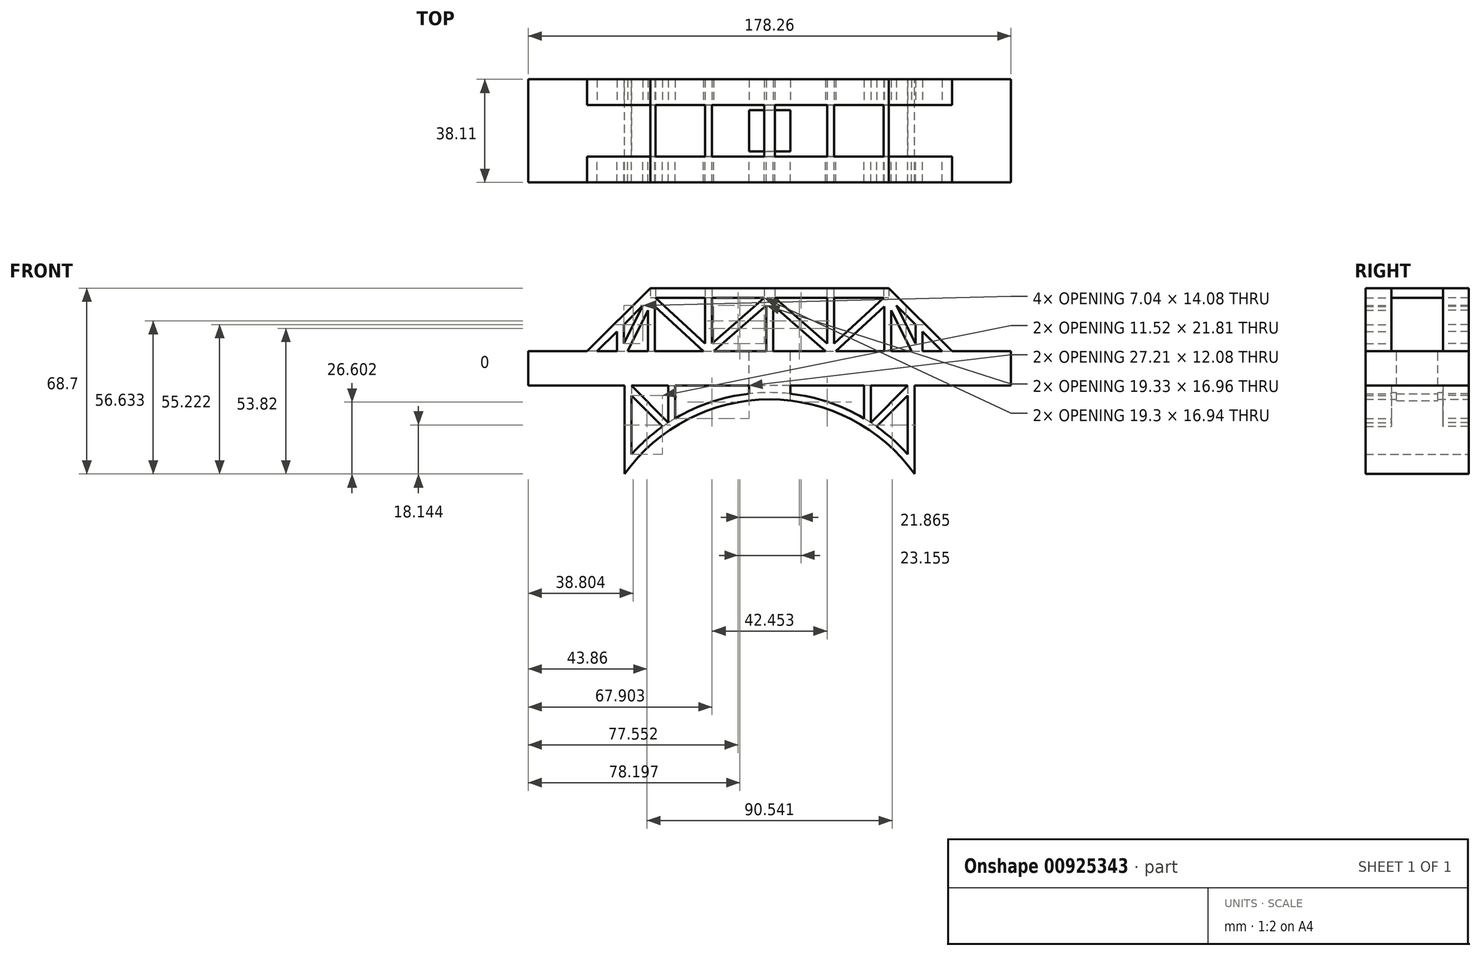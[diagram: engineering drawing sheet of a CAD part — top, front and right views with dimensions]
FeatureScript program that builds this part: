
annotation { "Feature Type Name" : "Feature", "Feature Type Description" : "" }
export const myFeature = defineFeature(function(context is Context, id is Id, definition is map)
    precondition{}
    {
        {
            var Q0;
            Q0=qCreatedBy(makeId("Front.planeOp"),FACE);
            var sketch = newSketch(context, id + "F0", { "sketchPlane" : qUnion([Q0])});
            skLineSegment(sketch, "E0.bottom", {"start": v(-63.73, 4.53) * mm, "end": v(63.73, 4.53) * mm});
            skLineSegment(sketch, "E1.bottom", {"start": v(-63.73, 4.53) * mm, "end": v(-89.13, 4.53) * mm});
            skLineSegment(sketch, "E1.top", {"start": v(-63.73, -8.17) * mm, "end": v(-89.13, -8.17) * mm});
            skLineSegment(sketch, "E1.left", {"start": v(-63.73, -3.37) * mm, "end": v(-63.73, -8.17) * mm});
            skLineSegment(sketch, "E1.right", {"start": v(-89.13, 4.53) * mm, "end": v(-89.13, -8.17) * mm});
            skPoint(sketch, "E2.oppositeSnap0", {"position": v(-76.43, -8.17) * mm});
            skLineSegment(sketch, "E2.bottom", {"start": v(63.73, 4.53) * mm, "end": v(89.13, 4.53) * mm});
            skLineSegment(sketch, "E2.top", {"start": v(63.73, -8.17) * mm, "end": v(89.13, -8.17) * mm});
            skLineSegment(sketch, "E2.left", {"start": v(63.73, 4.53) * mm, "end": v(63.73, -8.17) * mm});
            skLineSegment(sketch, "E2.right", {"start": v(89.13, 4.53) * mm, "end": v(89.13, -8.17) * mm});
            skPoint(sketch, "E3", {"position": v(-3.25, -27.46) * mm});
            skPoint(sketch, "E4", {"position": v(-24.97, -27.46) * mm});
            skPoint(sketch, "E5", {"position": v(18.48, -27.46) * mm});
            skPoint(sketch, "E6", {"position": v(0, -8.17) * mm});
            skPoint(sketch, "E7", {"position": v(-22.52, -8.17) * mm});
            skPoint(sketch, "E8", {"position": v(22.52, -8.17) * mm});
            skLineSegment(sketch, "E9", {"start": v(-43.58, -8.17) * mm, "end": v(-43.58, 4.53) * mm});
            skLineSegment(sketch, "E10", {"start": v(-22.52, -8.17) * mm, "end": v(-22.52, 4.53) * mm});
            skLineSegment(sketch, "E11", {"start": v(0, -8.17) * mm, "end": v(0, 4.53) * mm});
            skLineSegment(sketch, "E12", {"start": v(22.52, -8.17) * mm, "end": v(22.52, 4.53) * mm});
            skLineSegment(sketch, "E13", {"start": v(43.58, -8.17) * mm, "end": v(43.58, 4.53) * mm});
            skLineSegment(sketch, "E14", {"start": v(-63.73, 4.53) * mm, "end": v(-63.73, 4.53) * mm});
            skLineSegment(sketch, "E15", {"start": v(-63.73, -3.37) * mm, "end": v(-63.73, 4.53) * mm});
            skLineSegment(sketch, "E16", {"start": v(63.73, 4.53) * mm, "end": v(43.97, 24.3) * mm});
            skLineSegment(sketch, "E17", {"start": v(43.97, 24.3) * mm, "end": v(-43.97, 24.3) * mm});
            skLineSegment(sketch, "E18", {"start": v(-43.97, 24.3) * mm, "end": v(-63.73, 4.53) * mm});
            skLineSegment(sketch, "E19", {"start": v(-53.85, 14.41) * mm, "end": v(-53.85, 4.53) * mm});
            skLineSegment(sketch, "E20", {"start": v(-53.85, 4.53) * mm, "end": v(-43.97, 24.3) * mm});
            skLineSegment(sketch, "E21", {"start": v(53.85, 14.41) * mm, "end": v(53.85, 4.53) * mm});
            skLineSegment(sketch, "E22", {"start": v(43.97, 24.3) * mm, "end": v(53.85, 4.53) * mm});
            skLineSegment(sketch, "E23", {"start": v(43.97, 24.3) * mm, "end": v(22.52, 4.53) * mm});
            skLineSegment(sketch, "E24", {"start": v(0, 24.3) * mm, "end": v(22.52, 4.53) * mm});
            skLineSegment(sketch, "E25", {"start": v(-22.52, 4.53) * mm, "end": v(0, 24.3) * mm});
            skLineSegment(sketch, "E26", {"start": v(-43.97, 24.3) * mm, "end": v(-22.52, 4.53) * mm});
            skLineSegment(sketch, "E27.0", {"start": v(43.58, 22.22) * mm, "end": v(52.43, 4.53) * mm});
            skLineSegment(sketch, "E27.1", {"start": v(43.58, 22.22) * mm, "end": v(24.4, 4.53) * mm});
            skLineSegment(sketch, "E27.2", {"start": v(-52.43, 4.53) * mm, "end": v(-43.58, 22.22) * mm});
            skLineSegment(sketch, "E27.3", {"start": v(-43.58, 22.22) * mm, "end": v(-24.4, 4.53) * mm});
            skLineSegment(sketch, "E27.4", {"start": v(-20.6, 4.53) * mm, "end": v(0, 22.6) * mm});
            skLineSegment(sketch, "E27.5", {"start": v(0, 22.6) * mm, "end": v(20.6, 4.53) * mm});
            skLineSegment(sketch, "E28.0", {"start": v(42.1, 24.3) * mm, "end": v(22.5, 6.24) * mm});
            skLineSegment(sketch, "E28.1", {"start": v(1.93, 24.3) * mm, "end": v(22.5, 6.24) * mm});
            skLineSegment(sketch, "E28.2", {"start": v(-22.5, 6.24) * mm, "end": v(-1.93, 24.3) * mm});
            skLineSegment(sketch, "E28.3", {"start": v(-42.1, 24.3) * mm, "end": v(-22.5, 6.24) * mm});
            skLineSegment(sketch, "E29.0", {"start": v(-43.97, 27.89) * mm, "end": v(-67.32, 4.53) * mm});
            skLineSegment(sketch, "E30", {"start": v(-43.97, 27.89) * mm, "end": v(43.97, 27.89) * mm});
            skLineSegment(sketch, "E31.0", {"start": v(67.32, 4.53) * mm, "end": v(43.97, 27.89) * mm});
            skLineSegment(sketch, "E32", {"start": v(-43.58, 4.53) * mm, "end": v(-43.58, 22.22) * mm});
            skLineSegment(sketch, "E33", {"start": v(43.58, 22.22) * mm, "end": v(43.58, 4.53) * mm});
            skLineSegment(sketch, "E34", {"start": v(0, 22.6) * mm, "end": v(0, 4.53) * mm});
            skLineSegment(sketch, "E35", {"start": v(-22.5, 6.24) * mm, "end": v(-22.5, 24.3) * mm});
            skLineSegment(sketch, "E36", {"start": v(22.5, 6.24) * mm, "end": v(22.5, 24.3) * mm});
            skLineSegment(sketch, "E37.0", {"start": v(-21.23, 7.35) * mm, "end": v(-21.23, 24.3) * mm});
            skLineSegment(sketch, "E38.0", {"start": v(-23.77, 7.4) * mm, "end": v(-23.77, 24.3) * mm});
            skLineSegment(sketch, "E39.0", {"start": v(23.77, 7.4) * mm, "end": v(23.77, 24.3) * mm});
            skLineSegment(sketch, "E40.0", {"start": v(21.23, 7.35) * mm, "end": v(21.23, 24.3) * mm});
            skLineSegment(sketch, "E41.0", {"start": v(-42.31, 4.53) * mm, "end": v(-42.31, 21.05) * mm});
            skLineSegment(sketch, "E42.0", {"start": v(-44.85, 4.53) * mm, "end": v(-44.85, 19.68) * mm});
            skLineSegment(sketch, "E43.0", {"start": v(42.31, 21.05) * mm, "end": v(42.31, 4.53) * mm});
            skLineSegment(sketch, "E44.0", {"start": v(44.85, 19.68) * mm, "end": v(44.85, 4.53) * mm});
            skLineSegment(sketch, "E45", {"start": v(-23.77, 24.3) * mm, "end": v(-21.23, 24.3) * mm});
            skLineSegment(sketch, "E46", {"start": v(-23.77, 7.4) * mm, "end": v(-22.5, 6.24) * mm});
            skLineSegment(sketch, "E47", {"start": v(-22.5, 6.24) * mm, "end": v(-21.23, 7.35) * mm});
            skLineSegment(sketch, "E48.0", {"start": v(-1.27, 21.49) * mm, "end": v(-1.27, 4.52) * mm});
            skLineSegment(sketch, "E49.0", {"start": v(1.27, 21.49) * mm, "end": v(1.27, 4.52) * mm});
            skLineSegment(sketch, "E50.0", {"start": v(-56.39, 11.87) * mm, "end": v(-56.39, 4.53) * mm});
            skLineSegment(sketch, "E51.0", {"start": v(56.39, 11.87) * mm, "end": v(56.39, 4.53) * mm});
            skLineSegment(sketch, "E52.0", {"start": v(46.8, 21.45) * mm, "end": v(53.85, 7.37) * mm});
            skLineSegment(sketch, "E53", {"start": v(43.58, -8.17) * mm, "end": v(22.52, -8.17) * mm});
            skLineSegment(sketch, "E54", {"start": v(-63.73, -8.17) * mm, "end": v(-63.16, -8.17) * mm});
            skLineSegment(sketch, "E55", {"start": v(-63.16, -8.17) * mm, "end": v(-44.94, -8.17) * mm});
            skLineSegment(sketch, "E56", {"start": v(-43.58, -8.17) * mm, "end": v(-44.94, -8.17) * mm});
            skLineSegment(sketch, "E57", {"start": v(-42.31, -8.17) * mm, "end": v(-43.58, -8.17) * mm});
            skLineSegment(sketch, "E58", {"start": v(-42.31, -8.17) * mm, "end": v(-22.52, -8.17) * mm});
            skLineSegment(sketch, "E59", {"start": v(43.58, -8.17) * mm, "end": v(44.85, -8.17) * mm});
            skLineSegment(sketch, "E60", {"start": v(44.85, -8.17) * mm, "end": v(61.32, -8.17) * mm});
            skLineSegment(sketch, "E61", {"start": v(61.32, -8.17) * mm, "end": v(63.73, -8.17) * mm});
            skLineSegment(sketch, "E62", {"start": v(-22.52, -8.17) * mm, "end": v(-7.62, -8.17) * mm});
            skLineSegment(sketch, "E63", {"start": v(22.52, -8.17) * mm, "end": v(7.62, -8.17) * mm});
            skLineSegment(sketch, "E64", {"start": v(-7.62, -8.17) * mm, "end": v(-7.62, 4.53) * mm});
            skLineSegment(sketch, "E65", {"start": v(7.62, -8.17) * mm, "end": v(7.62, 4.53) * mm});
            skLineSegment(sketch, "E66.0", {"start": v(-53.85, 7.37) * mm, "end": v(-46.8, 21.45) * mm});
            skLineSegment(sketch, "E67", {"start": v(-51.03, -8.17) * mm, "end": v(-51.03, -33.57) * mm});
            skLineSegment(sketch, "E68", {"start": v(51.03, -8.17) * mm, "end": v(51.03, -33.57) * mm});
            skArc(sketch, "E69", {"start": v(51.03, -33.57) * mm, "mid": v(0, -10.7) * mm, "end": v(-51.03, -33.57) * mm});
            skLineSegment(sketch, "E70.0", {"start": v(-53.57, -8.17) * mm, "end": v(-53.57, -40.8) * mm});
            skArc(sketch, "E70.1", {"start": v(53.57, -40.8) * mm, "mid": v(0, -13.25) * mm, "end": v(-53.57, -40.8) * mm});
            skLineSegment(sketch, "E70.2", {"start": v(53.57, -8.17) * mm, "end": v(53.57, -40.8) * mm});
            skLineSegment(sketch, "E71", {"start": v(-51.03, -8.17) * mm, "end": v(-37.37, -21.83) * mm});
            skLineSegment(sketch, "E72", {"start": v(-37.37, -21.83) * mm, "end": v(-37.37, -8.17) * mm});
            skLineSegment(sketch, "E73", {"start": v(37.37, -8.17) * mm, "end": v(37.37, -21.83) * mm});
            skLineSegment(sketch, "E74", {"start": v(37.37, -21.83) * mm, "end": v(51.03, -8.17) * mm});
            skLineSegment(sketch, "E75", {"start": v(-7.62, -8.17) * mm, "end": v(7.62, -8.17) * mm});
            skLineSegment(sketch, "E76.0", {"start": v(34.83, -8.17) * mm, "end": v(34.83, -20.25) * mm});
            skLineSegment(sketch, "E77.0", {"start": v(39.51, -23.28) * mm, "end": v(51.03, -11.76) * mm});
            skLineSegment(sketch, "E78.0", {"start": v(-34.83, -20.25) * mm, "end": v(-34.83, -8.17) * mm});
            skLineSegment(sketch, "E79.0", {"start": v(-51.03, -11.76) * mm, "end": v(-39.51, -23.28) * mm});
            skLineSegment(sketch, "E80", {"start": v(-22.52, -8.17) * mm, "end": v(-17.66, -13.03) * mm});
            skLineSegment(sketch, "E81", {"start": v(22.52, -8.17) * mm, "end": v(17.66, -13.03) * mm});
            skLineSegment(sketch, "E82", {"start": v(-7.62, -8.17) * mm, "end": v(-7.62, -11.14) * mm});
            skLineSegment(sketch, "E83", {"start": v(7.62, -8.17) * mm, "end": v(7.62, -11.14) * mm});
            skSolve(sketch);
        }
        {
            var Q0;
            Q0=makeQuery(id+"F0.imprint","IMPRINT",FACE,{"disambiguationData":[TD([[makeQuery(id+"F0.imprint","IMPRINT",EDGE,{"derivedFrom":sQuery(id+"F0.wireOp",EDGE,"E1.top")}),-1.0]])]});
            var Q1;
            Q1=makeQuery(id+"F0.imprint","IMPRINT",FACE,{"disambiguationData":[TD([[makeQuery(id+"F0.imprint","IMPRINT",EDGE,{"derivedFrom":sQuery(id+"F0.wireOp",EDGE,"E2.top")}),1.0]])]});
            extrude(context, id + "F1", {"entities" : qUnion([Q0, Q1]), "endBound" : BoundingType.SYMMETRIC, "depth" : 19.05 * mm, "offsetDistance" : 25.4 * mm});
        }
        {
            var Q0;
            Q0=makeQuery(id+"F0.imprint","IMPRINT",FACE,{"disambiguationData":[TD([[makeQuery(id+"F0.imprint","IMPRINT",EDGE,{"derivedFrom":sQuery(id+"F0.wireOp",EDGE,"E1.left")}),1.0]])]});
            var Q1;
            {var subQ0=sQuery(id+"F0.wireOp",EDGE,"E9");Q1=makeQuery(id+"F0.imprint","IMPRINT",FACE,{"disambiguationData":[TD([[makeQuery(id+"F0.imprint","IMPRINT",EDGE,{"derivedFrom":subQ0}),-1.0]])]});}
            var Q2;
            {var subQ0=sQuery(id+"F0.wireOp",EDGE,"E12");Q2=makeQuery(id+"F0.imprint","IMPRINT",FACE,{"disambiguationData":[TD([[makeQuery(id+"F0.imprint","IMPRINT",EDGE,{"derivedFrom":subQ0}),-1.0]])]});}
            var Q3;
            {var subQ8=sQuery(id+"F0.wireOp",EDGE,"E2.left");Q3=makeQuery(id+"F0.imprint","IMPRINT",FACE,{"disambiguationData":[TD([[makeQuery(id+"F0.imprint","IMPRINT",EDGE,{"derivedFrom":subQ8}),-1.0]])]});}
            var Q4;
            {var subQ0=sQuery(id+"F0.wireOp",EDGE,"E10");Q4=makeQuery(id+"F0.imprint","IMPRINT",FACE,{"disambiguationData":[TD([[makeQuery(id+"F0.imprint","IMPRINT",EDGE,{"derivedFrom":subQ0}),-1.0]])]});}
            var Q5;
            {var subQ0=sQuery(id+"F0.wireOp",EDGE,"E12");Q5=makeQuery(id+"F0.imprint","IMPRINT",FACE,{"disambiguationData":[TD([[makeQuery(id+"F0.imprint","IMPRINT",EDGE,{"derivedFrom":subQ0}),1.0]])]});}
            extrude(context, id + "F2", {"entities" : qUnion([Q0, Q1, Q2, Q3, Q4, Q5]), "operationType" : NewBodyOperationType.ADD, "endBound" : BoundingType.SYMMETRIC, "depth" : 19.05 * mm, "offsetDistance" : 25.4 * mm});
        }
        {
            var Q0;
            Q0=makeQuery(id+"F0.imprint","IMPRINT",FACE,{"disambiguationData":[TD([[makeQuery(id+"F0.imprint","IMPRINT",EDGE,{"derivedFrom":sQuery(id+"F0.wireOp",EDGE,"E1.left")}),1.0]])]});
            var Q1;
            {var subQ0=sQuery(id+"F0.wireOp",EDGE,"E9");Q1=makeQuery(id+"F0.imprint","IMPRINT",FACE,{"disambiguationData":[TD([[makeQuery(id+"F0.imprint","IMPRINT",EDGE,{"derivedFrom":subQ0}),-1.0]])]});}
            var Q2;
            {var subQ0=sQuery(id+"F0.wireOp",EDGE,"E10");Q2=makeQuery(id+"F0.imprint","IMPRINT",FACE,{"disambiguationData":[TD([[makeQuery(id+"F0.imprint","IMPRINT",EDGE,{"derivedFrom":subQ0}),-1.0]])]});}
            var Q3;
            {var subQ1=sQuery(id+"F0.wireOp",EDGE,"E11");Q3=makeQuery(id+"F0.imprint","IMPRINT",FACE,{"disambiguationData":[TD([[makeQuery(id+"F0.imprint","IMPRINT",EDGE,{"derivedFrom":subQ1}),-1.0]])]});}
            var Q4;
            {var subQ0=sQuery(id+"F0.wireOp",EDGE,"E12");Q4=makeQuery(id+"F0.imprint","IMPRINT",FACE,{"disambiguationData":[TD([[makeQuery(id+"F0.imprint","IMPRINT",EDGE,{"derivedFrom":subQ0}),-1.0]])]});}
            var Q5;
            {var subQ8=sQuery(id+"F0.wireOp",EDGE,"E2.left");Q5=makeQuery(id+"F0.imprint","IMPRINT",FACE,{"disambiguationData":[TD([[makeQuery(id+"F0.imprint","IMPRINT",EDGE,{"derivedFrom":subQ8}),-1.0]])]});}
            extrude(context, id + "F3", {"entities" : qUnion([Q0, Q1, Q2, Q3, Q4, Q5]), "operationType" : NewBodyOperationType.ADD, "endBound" : BoundingType.SYMMETRIC, "depth" : 7.62 * mm, "offsetDistance" : 25.4 * mm});
        }
        {
            var Q0;
            {var subQ7=sQuery(id+"F0.wireOp",EDGE,"E24");Q0=makeQuery(id+"F0.imprint","IMPRINT",FACE,{"disambiguationData":[TD([[makeQuery(id+"F0.imprint","IMPRINT",EDGE,{"derivedFrom":subQ7}),-1.0]])]});}
            var Q1;
            {var subQ4=sQuery(id+"F0.wireOp",EDGE,"E25");Q1=makeQuery(id+"F0.imprint","IMPRINT",FACE,{"disambiguationData":[TD([[makeQuery(id+"F0.imprint","IMPRINT",EDGE,{"derivedFrom":subQ4}),1.0]])]});}
            var Q2;
            {var subQ4=sQuery(id+"F0.wireOp",EDGE,"E25");Q2=makeQuery(id+"F0.imprint","IMPRINT",FACE,{"disambiguationData":[TD([[makeQuery(id+"F0.imprint","IMPRINT",EDGE,{"derivedFrom":subQ4}),1.0]])]});}
            var Q3;
            {var subQ1=sQuery(id+"F0.wireOp",EDGE,"E20");Q3=makeQuery(id+"F0.imprint","IMPRINT",FACE,{"disambiguationData":[TD([[makeQuery(id+"F0.imprint","IMPRINT",EDGE,{"derivedFrom":subQ1}),-1.0]])]});}
            var Q4;
            {var subQ1=sQuery(id+"F0.wireOp",EDGE,"E20");Q4=makeQuery(id+"F0.imprint","IMPRINT",FACE,{"disambiguationData":[TD([[makeQuery(id+"F0.imprint","IMPRINT",EDGE,{"derivedFrom":subQ1}),-1.0]])]});}
            var Q5;
            {var subQ1=sQuery(id+"F0.wireOp",EDGE,"E23");Q5=makeQuery(id+"F0.imprint","IMPRINT",FACE,{"disambiguationData":[TD([[makeQuery(id+"F0.imprint","IMPRINT",EDGE,{"derivedFrom":subQ1}),-1.0]])]});}
            var Q6;
            {var subQ7=sQuery(id+"F0.wireOp",EDGE,"E24");Q6=makeQuery(id+"F0.imprint","IMPRINT",FACE,{"disambiguationData":[TD([[makeQuery(id+"F0.imprint","IMPRINT",EDGE,{"derivedFrom":subQ7}),-1.0]])]});}
            var Q7;
            {var subQ0=sQuery(id+"F0.wireOp",EDGE,"E22");Q7=makeQuery(id+"F0.imprint","IMPRINT",FACE,{"disambiguationData":[TD([[makeQuery(id+"F0.imprint","IMPRINT",EDGE,{"derivedFrom":subQ0}),-1.0]])]});}
            var Q8;
            {var subQ1=sQuery(id+"F0.wireOp",EDGE,"E23");Q8=makeQuery(id+"F0.imprint","IMPRINT",FACE,{"disambiguationData":[TD([[makeQuery(id+"F0.imprint","IMPRINT",EDGE,{"derivedFrom":subQ1}),-1.0]])]});}
            var Q9;
            {var subQ0=sQuery(id+"F0.wireOp",EDGE,"E22");Q9=makeQuery(id+"F0.imprint","IMPRINT",FACE,{"disambiguationData":[TD([[makeQuery(id+"F0.imprint","IMPRINT",EDGE,{"derivedFrom":subQ0}),-1.0]])]});}
            var Q10;
            {var subQ0=sQuery(id+"F0.wireOp",EDGE,"E15");var subQ1=sQuery(id+"F0.wireOp",EDGE,"E1.left");Q10=makeQuery(id+"F2.boolean.opBoolean","MERGE",FACE,{"derivedFrom":[makeQuery(id+"F1.opExtrude","CAP_FACE",FACE,{"disambiguationData":[OSD([sQuery(id+"F0.wireOp",EDGE,"E1.bottom"),sQuery(id+"F0.wireOp",EDGE,"E1.top"),subQ1,sQuery(id+"F0.wireOp",EDGE,"E1.right"),subQ0])],"isStart":false}),makeQuery(id+"F2.opExtrude","CAP_FACE",FACE,{"disambiguationData":[OSD([sQuery(id+"F0.wireOp",EDGE,"E0.bottom"),subQ1,subQ0,sQuery(id+"F0.wireOp",EDGE,"E54"),sQuery(id+"F0.wireOp",EDGE,"E55"),sQuery(id+"F0.wireOp",EDGE,"E56"),sQuery(id+"F0.wireOp",EDGE,"E57"),sQuery(id+"F0.wireOp",EDGE,"E58"),sQuery(id+"F0.wireOp",EDGE,"E62"),sQuery(id+"F0.wireOp",EDGE,"E64")])],"isStart":false})]});}
            extrude(context, id + "F4", {"entities" : qUnion([Q0, Q1, Q2, Q3, Q4, Q5, Q6, Q7, Q8, Q9]), "operationType" : NewBodyOperationType.ADD, "endBound" : BoundingType.UP_TO_SURFACE, "depth" : 12.7 * mm, "endBoundEntityFace" : qUnion([Q10]), "offsetDistance" : 25.4 * mm});
        }
        {
            var Q0;
            {var subQ28=sQuery(id+"F0.wireOp",EDGE,"E29.0");Q0=makeQuery(id+"F0.imprint","IMPRINT",FACE,{"disambiguationData":[TD([[makeQuery(id+"F0.imprint","IMPRINT",EDGE,{"derivedFrom":subQ28}),1.0]])]});}
            var Q1;
            {var subQ0=sQuery(id+"F0.wireOp",EDGE,"E0.bottom");var subQ1=sQuery(id+"F0.wireOp",EDGE,"E15");var subQ2=sQuery(id+"F0.wireOp",EDGE,"E1.left");Q1=makeQuery(id+"F4.boolean.opBoolean","MERGE",FACE,{"derivedFrom":[makeQuery(id+"F2.boolean.opBoolean","MERGE",FACE,{"derivedFrom":[makeQuery(id+"F1.opExtrude","CAP_FACE",FACE,{"disambiguationData":[OSD([sQuery(id+"F0.wireOp",EDGE,"E1.bottom"),sQuery(id+"F0.wireOp",EDGE,"E1.top"),subQ2,sQuery(id+"F0.wireOp",EDGE,"E1.right"),subQ1])],"isStart":false}),makeQuery(id+"F2.opExtrude","CAP_FACE",FACE,{"disambiguationData":[OSD([subQ0,subQ2,subQ1,sQuery(id+"F0.wireOp",EDGE,"E54"),sQuery(id+"F0.wireOp",EDGE,"E55"),sQuery(id+"F0.wireOp",EDGE,"E56"),sQuery(id+"F0.wireOp",EDGE,"E57"),sQuery(id+"F0.wireOp",EDGE,"E58"),sQuery(id+"F0.wireOp",EDGE,"E62"),sQuery(id+"F0.wireOp",EDGE,"E64")])],"isStart":false})]}),makeQuery(id+"F4.opExtrude","CAP_FACE",FACE,{"disambiguationData":[OSD([subQ0,sQuery(id+"F0.wireOp",EDGE,"E17"),sQuery(id+"F0.wireOp",EDGE,"E20"),sQuery(id+"F0.wireOp",EDGE,"E22"),sQuery(id+"F0.wireOp",EDGE,"E27.0"),sQuery(id+"F0.wireOp",EDGE,"E27.1"),sQuery(id+"F0.wireOp",EDGE,"E27.2"),sQuery(id+"F0.wireOp",EDGE,"E27.3"),sQuery(id+"F0.wireOp",EDGE,"E27.4"),sQuery(id+"F0.wireOp",EDGE,"E27.5"),sQuery(id+"F0.wireOp",EDGE,"E28.0"),sQuery(id+"F0.wireOp",EDGE,"E28.1"),sQuery(id+"F0.wireOp",EDGE,"E28.2"),sQuery(id+"F0.wireOp",EDGE,"E28.3")])],"isStart":false})]});}
            extrude(context, id + "F5", {"entities" : qUnion([Q0]), "operationType" : NewBodyOperationType.ADD, "endBound" : BoundingType.UP_TO_SURFACE, "depth" : 12.7 * mm, "endBoundEntityFace" : qUnion([Q1]), "offsetDistance" : 25.4 * mm});
        }
        {
            var Q0;
            {var subQ0=sQuery(id+"F0.wireOp",EDGE,"E35");Q0=makeQuery(id+"F0.imprint","IMPRINT",FACE,{"disambiguationData":[TD([[makeQuery(id+"F0.imprint","IMPRINT",EDGE,{"derivedFrom":subQ0}),1.0]])]});}
            var Q1;
            {var subQ0=sQuery(id+"F0.wireOp",EDGE,"E35");Q1=makeQuery(id+"F0.imprint","IMPRINT",FACE,{"disambiguationData":[TD([[makeQuery(id+"F0.imprint","IMPRINT",EDGE,{"derivedFrom":subQ0}),-1.0]])]});}
            var Q2;
            {var subQ2=sQuery(id+"F0.wireOp",EDGE,"E32");Q2=makeQuery(id+"F0.imprint","IMPRINT",FACE,{"disambiguationData":[TD([[makeQuery(id+"F0.imprint","IMPRINT",EDGE,{"derivedFrom":subQ2}),-1.0]])]});}
            var Q3;
            {var subQ0=sQuery(id+"F0.wireOp",EDGE,"E32");Q3=makeQuery(id+"F0.imprint","IMPRINT",FACE,{"disambiguationData":[TD([[makeQuery(id+"F0.imprint","IMPRINT",EDGE,{"derivedFrom":subQ0}),1.0]])]});}
            var Q4;
            {var subQ2=sQuery(id+"F0.wireOp",EDGE,"E36");Q4=makeQuery(id+"F0.imprint","IMPRINT",FACE,{"disambiguationData":[TD([[makeQuery(id+"F0.imprint","IMPRINT",EDGE,{"derivedFrom":subQ2}),1.0]])]});}
            var Q5;
            {var subQ0=sQuery(id+"F0.wireOp",EDGE,"E36");Q5=makeQuery(id+"F0.imprint","IMPRINT",FACE,{"disambiguationData":[TD([[makeQuery(id+"F0.imprint","IMPRINT",EDGE,{"derivedFrom":subQ0}),-1.0]])]});}
            var Q6;
            {var subQ0=sQuery(id+"F0.wireOp",EDGE,"E33");Q6=makeQuery(id+"F0.imprint","IMPRINT",FACE,{"disambiguationData":[TD([[makeQuery(id+"F0.imprint","IMPRINT",EDGE,{"derivedFrom":subQ0}),1.0]])]});}
            var Q7;
            {var subQ0=sQuery(id+"F0.wireOp",EDGE,"E33");Q7=makeQuery(id+"F0.imprint","IMPRINT",FACE,{"disambiguationData":[TD([[makeQuery(id+"F0.imprint","IMPRINT",EDGE,{"derivedFrom":subQ0}),-1.0]])]});}
            var Q8;
            {var subQ0=sQuery(id+"F0.wireOp",EDGE,"E17");var subQ1=sQuery(id+"F0.wireOp",EDGE,"E1.bottom");var subQ2=sQuery(id+"F0.wireOp",EDGE,"E0.bottom");var subQ3=sQuery(id+"F0.wireOp",EDGE,"E15");var subQ4=sQuery(id+"F0.wireOp",EDGE,"E1.left");Q8=makeQuery(id+"F5.boolean.opBoolean","MERGE",FACE,{"derivedFrom":[makeQuery(id+"F4.boolean.opBoolean","MERGE",FACE,{"derivedFrom":[makeQuery(id+"F2.boolean.opBoolean","MERGE",FACE,{"derivedFrom":[makeQuery(id+"F1.opExtrude","CAP_FACE",FACE,{"disambiguationData":[OSD([subQ1,sQuery(id+"F0.wireOp",EDGE,"E1.top"),subQ4,sQuery(id+"F0.wireOp",EDGE,"E1.right"),subQ3])],"isStart":false}),makeQuery(id+"F2.opExtrude","CAP_FACE",FACE,{"disambiguationData":[OSD([subQ2,subQ4,subQ3,sQuery(id+"F0.wireOp",EDGE,"E54"),sQuery(id+"F0.wireOp",EDGE,"E55"),sQuery(id+"F0.wireOp",EDGE,"E56"),sQuery(id+"F0.wireOp",EDGE,"E57"),sQuery(id+"F0.wireOp",EDGE,"E58"),sQuery(id+"F0.wireOp",EDGE,"E62"),sQuery(id+"F0.wireOp",EDGE,"E64")])],"isStart":false})]}),makeQuery(id+"F4.opExtrude","CAP_FACE",FACE,{"disambiguationData":[OSD([subQ2,subQ0,sQuery(id+"F0.wireOp",EDGE,"E20"),sQuery(id+"F0.wireOp",EDGE,"E22"),sQuery(id+"F0.wireOp",EDGE,"E27.0"),sQuery(id+"F0.wireOp",EDGE,"E27.1"),sQuery(id+"F0.wireOp",EDGE,"E27.2"),sQuery(id+"F0.wireOp",EDGE,"E27.3"),sQuery(id+"F0.wireOp",EDGE,"E27.4"),sQuery(id+"F0.wireOp",EDGE,"E27.5"),sQuery(id+"F0.wireOp",EDGE,"E28.0"),sQuery(id+"F0.wireOp",EDGE,"E28.1"),sQuery(id+"F0.wireOp",EDGE,"E28.2"),sQuery(id+"F0.wireOp",EDGE,"E28.3")])],"isStart":false})]}),makeQuery(id+"F5.opExtrude","CAP_FACE",FACE,{"disambiguationData":[OSD([subQ1,sQuery(id+"F0.wireOp",EDGE,"E2.bottom"),sQuery(id+"F0.wireOp",EDGE,"E16"),subQ0,sQuery(id+"F0.wireOp",EDGE,"E18"),sQuery(id+"F0.wireOp",EDGE,"E29.0"),sQuery(id+"F0.wireOp",EDGE,"E30"),sQuery(id+"F0.wireOp",EDGE,"E31.0")])],"isStart":false})]});}
            extrude(context, id + "F6", {"entities" : qUnion([Q0, Q1, Q2, Q3, Q4, Q5, Q6, Q7]), "operationType" : NewBodyOperationType.ADD, "endBound" : BoundingType.UP_TO_SURFACE, "depth" : 12.7 * mm, "endBoundEntityFace" : qUnion([Q8]), "offsetDistance" : 25.4 * mm});
        }
        {
            var Q0;
            {var subQ0=sQuery(id+"F0.wireOp",EDGE,"E34");Q0=makeQuery(id+"F0.imprint","IMPRINT",FACE,{"disambiguationData":[TD([[makeQuery(id+"F0.imprint","IMPRINT",EDGE,{"derivedFrom":subQ0}),-1.0]])]});}
            var Q1;
            {var subQ0=sQuery(id+"F0.wireOp",EDGE,"E34");Q1=makeQuery(id+"F0.imprint","IMPRINT",FACE,{"disambiguationData":[TD([[makeQuery(id+"F0.imprint","IMPRINT",EDGE,{"derivedFrom":subQ0}),1.0]])]});}
            var Q2;
            {var subQ0=sQuery(id+"F0.wireOp",EDGE,"E28.1");var subQ1=sQuery(id+"F0.wireOp",EDGE,"E28.0");var subQ2=sQuery(id+"F0.wireOp",EDGE,"E17");var subQ3=sQuery(id+"F0.wireOp",EDGE,"E28.3");var subQ4=sQuery(id+"F0.wireOp",EDGE,"E28.2");var subQ5=sQuery(id+"F0.wireOp",EDGE,"E27.1");var subQ6=sQuery(id+"F0.wireOp",EDGE,"E27.0");var subQ7=sQuery(id+"F0.wireOp",EDGE,"E0.bottom");var subQ8=sQuery(id+"F0.wireOp",EDGE,"E27.3");var subQ9=sQuery(id+"F0.wireOp",EDGE,"E27.2");var subQ10=sQuery(id+"F0.wireOp",EDGE,"E2.bottom");var subQ11=sQuery(id+"F0.wireOp",EDGE,"E1.bottom");var subQ12=sQuery(id+"F0.wireOp",EDGE,"E15");var subQ13=sQuery(id+"F0.wireOp",EDGE,"E1.left");var subQ14=sQuery(id+"F0.wireOp",EDGE,"E2.left");Q2=makeQuery(id+"F6.boolean.opBoolean","MERGE",FACE,{"derivedFrom":[makeQuery(id+"F2.boolean.opBoolean","MERGE",FACE,{"derivedFrom":[makeQuery(id+"F1.opExtrude","CAP_FACE",FACE,{"disambiguationData":[OSD([subQ10,sQuery(id+"F0.wireOp",EDGE,"E2.top"),subQ14,sQuery(id+"F0.wireOp",EDGE,"E2.right")])],"isStart":false}),makeQuery(id+"F2.opExtrude","CAP_FACE",FACE,{"disambiguationData":[OSD([subQ7,subQ14,sQuery(id+"F0.wireOp",EDGE,"E53"),sQuery(id+"F0.wireOp",EDGE,"E59"),sQuery(id+"F0.wireOp",EDGE,"E60"),sQuery(id+"F0.wireOp",EDGE,"E61"),sQuery(id+"F0.wireOp",EDGE,"E63"),sQuery(id+"F0.wireOp",EDGE,"E65")])],"isStart":false})]}),makeQuery(id+"F5.boolean.opBoolean","MERGE",FACE,{"derivedFrom":[makeQuery(id+"F4.boolean.opBoolean","MERGE",FACE,{"derivedFrom":[makeQuery(id+"F2.boolean.opBoolean","MERGE",FACE,{"derivedFrom":[makeQuery(id+"F1.opExtrude","CAP_FACE",FACE,{"disambiguationData":[OSD([subQ11,sQuery(id+"F0.wireOp",EDGE,"E1.top"),subQ13,sQuery(id+"F0.wireOp",EDGE,"E1.right"),subQ12])],"isStart":false}),makeQuery(id+"F2.opExtrude","CAP_FACE",FACE,{"disambiguationData":[OSD([subQ7,subQ13,subQ12,sQuery(id+"F0.wireOp",EDGE,"E54"),sQuery(id+"F0.wireOp",EDGE,"E55"),sQuery(id+"F0.wireOp",EDGE,"E56"),sQuery(id+"F0.wireOp",EDGE,"E57"),sQuery(id+"F0.wireOp",EDGE,"E58"),sQuery(id+"F0.wireOp",EDGE,"E62"),sQuery(id+"F0.wireOp",EDGE,"E64")])],"isStart":false})]}),makeQuery(id+"F4.opExtrude","CAP_FACE",FACE,{"disambiguationData":[OSD([subQ7,subQ2,sQuery(id+"F0.wireOp",EDGE,"E20"),sQuery(id+"F0.wireOp",EDGE,"E22"),subQ6,subQ5,subQ9,subQ8,sQuery(id+"F0.wireOp",EDGE,"E27.4"),sQuery(id+"F0.wireOp",EDGE,"E27.5"),subQ1,subQ0,subQ4,subQ3])],"isStart":false})]}),makeQuery(id+"F5.opExtrude","CAP_FACE",FACE,{"disambiguationData":[OSD([subQ11,subQ10,sQuery(id+"F0.wireOp",EDGE,"E16"),subQ2,sQuery(id+"F0.wireOp",EDGE,"E18"),sQuery(id+"F0.wireOp",EDGE,"E29.0"),sQuery(id+"F0.wireOp",EDGE,"E30"),sQuery(id+"F0.wireOp",EDGE,"E31.0")])],"isStart":false})]}),makeQuery(id+"F6.opExtrude","CAP_FACE",FACE,{"disambiguationData":[OSD([subQ7,subQ9,subQ8,sQuery(id+"F0.wireOp",EDGE,"E41.0"),sQuery(id+"F0.wireOp",EDGE,"E42.0")])],"isStart":false}),makeQuery(id+"F6.opExtrude","CAP_FACE",FACE,{"disambiguationData":[OSD([subQ7,subQ6,subQ5,sQuery(id+"F0.wireOp",EDGE,"E43.0"),sQuery(id+"F0.wireOp",EDGE,"E44.0")])],"isStart":false}),makeQuery(id+"F6.opExtrude","CAP_FACE",FACE,{"disambiguationData":[OSD([subQ2,subQ4,subQ3,sQuery(id+"F0.wireOp",EDGE,"E37.0"),sQuery(id+"F0.wireOp",EDGE,"E38.0")])],"isStart":false}),makeQuery(id+"F6.opExtrude","CAP_FACE",FACE,{"disambiguationData":[OSD([subQ2,subQ1,subQ0,sQuery(id+"F0.wireOp",EDGE,"E39.0"),sQuery(id+"F0.wireOp",EDGE,"E40.0")])],"isStart":false})]});}
            extrude(context, id + "F7", {"entities" : qUnion([Q0, Q1]), "operationType" : NewBodyOperationType.ADD, "endBound" : BoundingType.UP_TO_SURFACE, "depth" : 12.7 * mm, "endBoundEntityFace" : qUnion([Q2]), "offsetDistance" : 25.4 * mm});
        }
        {
            var Q0;
            {var subQ6=sQuery(id+"F0.wireOp",EDGE,"E51.0");Q0=makeQuery(id+"F0.imprint","IMPRINT",FACE,{"disambiguationData":[TD([[makeQuery(id+"F0.imprint","IMPRINT",EDGE,{"derivedFrom":subQ6}),-1.0]])]});}
            var Q1;
            {var subQ4=sQuery(id+"F0.wireOp",EDGE,"E50.0");Q1=makeQuery(id+"F0.imprint","IMPRINT",FACE,{"disambiguationData":[TD([[makeQuery(id+"F0.imprint","IMPRINT",EDGE,{"derivedFrom":subQ4}),1.0]])]});}
            var Q2;
            {var subQ0=sQuery(id+"F0.wireOp",EDGE,"E27.5");var subQ1=sQuery(id+"F0.wireOp",EDGE,"E27.4");var subQ2=sQuery(id+"F0.wireOp",EDGE,"E0.bottom");var subQ3=sQuery(id+"F0.wireOp",EDGE,"E28.1");var subQ4=sQuery(id+"F0.wireOp",EDGE,"E28.0");var subQ5=sQuery(id+"F0.wireOp",EDGE,"E17");var subQ6=sQuery(id+"F0.wireOp",EDGE,"E28.3");var subQ7=sQuery(id+"F0.wireOp",EDGE,"E28.2");var subQ8=sQuery(id+"F0.wireOp",EDGE,"E27.1");var subQ9=sQuery(id+"F0.wireOp",EDGE,"E27.0");var subQ10=sQuery(id+"F0.wireOp",EDGE,"E27.3");var subQ11=sQuery(id+"F0.wireOp",EDGE,"E27.2");var subQ12=sQuery(id+"F0.wireOp",EDGE,"E2.bottom");var subQ13=sQuery(id+"F0.wireOp",EDGE,"E1.bottom");var subQ14=sQuery(id+"F0.wireOp",EDGE,"E15");var subQ15=sQuery(id+"F0.wireOp",EDGE,"E1.left");var subQ16=sQuery(id+"F0.wireOp",EDGE,"E2.left");Q2=makeQuery(id+"F7.boolean.opBoolean","MERGE",FACE,{"derivedFrom":[makeQuery(id+"F6.boolean.opBoolean","MERGE",FACE,{"derivedFrom":[makeQuery(id+"F2.boolean.opBoolean","MERGE",FACE,{"derivedFrom":[makeQuery(id+"F1.opExtrude","CAP_FACE",FACE,{"disambiguationData":[OSD([subQ12,sQuery(id+"F0.wireOp",EDGE,"E2.top"),subQ16,sQuery(id+"F0.wireOp",EDGE,"E2.right")])],"isStart":false}),makeQuery(id+"F2.opExtrude","CAP_FACE",FACE,{"disambiguationData":[OSD([subQ2,subQ16,sQuery(id+"F0.wireOp",EDGE,"E53"),sQuery(id+"F0.wireOp",EDGE,"E59"),sQuery(id+"F0.wireOp",EDGE,"E60"),sQuery(id+"F0.wireOp",EDGE,"E61"),sQuery(id+"F0.wireOp",EDGE,"E63"),sQuery(id+"F0.wireOp",EDGE,"E65")])],"isStart":false})]}),makeQuery(id+"F5.boolean.opBoolean","MERGE",FACE,{"derivedFrom":[makeQuery(id+"F4.boolean.opBoolean","MERGE",FACE,{"derivedFrom":[makeQuery(id+"F2.boolean.opBoolean","MERGE",FACE,{"derivedFrom":[makeQuery(id+"F1.opExtrude","CAP_FACE",FACE,{"disambiguationData":[OSD([subQ13,sQuery(id+"F0.wireOp",EDGE,"E1.top"),subQ15,sQuery(id+"F0.wireOp",EDGE,"E1.right"),subQ14])],"isStart":false}),makeQuery(id+"F2.opExtrude","CAP_FACE",FACE,{"disambiguationData":[OSD([subQ2,subQ15,subQ14,sQuery(id+"F0.wireOp",EDGE,"E54"),sQuery(id+"F0.wireOp",EDGE,"E55"),sQuery(id+"F0.wireOp",EDGE,"E56"),sQuery(id+"F0.wireOp",EDGE,"E57"),sQuery(id+"F0.wireOp",EDGE,"E58"),sQuery(id+"F0.wireOp",EDGE,"E62"),sQuery(id+"F0.wireOp",EDGE,"E64")])],"isStart":false})]}),makeQuery(id+"F4.opExtrude","CAP_FACE",FACE,{"disambiguationData":[OSD([subQ2,subQ5,sQuery(id+"F0.wireOp",EDGE,"E20"),sQuery(id+"F0.wireOp",EDGE,"E22"),subQ9,subQ8,subQ11,subQ10,subQ1,subQ0,subQ4,subQ3,subQ7,subQ6])],"isStart":false})]}),makeQuery(id+"F5.opExtrude","CAP_FACE",FACE,{"disambiguationData":[OSD([subQ13,subQ12,sQuery(id+"F0.wireOp",EDGE,"E16"),subQ5,sQuery(id+"F0.wireOp",EDGE,"E18"),sQuery(id+"F0.wireOp",EDGE,"E29.0"),sQuery(id+"F0.wireOp",EDGE,"E30"),sQuery(id+"F0.wireOp",EDGE,"E31.0")])],"isStart":false})]}),makeQuery(id+"F6.opExtrude","CAP_FACE",FACE,{"disambiguationData":[OSD([subQ2,subQ11,subQ10,sQuery(id+"F0.wireOp",EDGE,"E41.0"),sQuery(id+"F0.wireOp",EDGE,"E42.0")])],"isStart":false}),makeQuery(id+"F6.opExtrude","CAP_FACE",FACE,{"disambiguationData":[OSD([subQ2,subQ9,subQ8,sQuery(id+"F0.wireOp",EDGE,"E43.0"),sQuery(id+"F0.wireOp",EDGE,"E44.0")])],"isStart":false}),makeQuery(id+"F6.opExtrude","CAP_FACE",FACE,{"disambiguationData":[OSD([subQ5,subQ7,subQ6,sQuery(id+"F0.wireOp",EDGE,"E37.0"),sQuery(id+"F0.wireOp",EDGE,"E38.0")])],"isStart":false}),makeQuery(id+"F6.opExtrude","CAP_FACE",FACE,{"disambiguationData":[OSD([subQ5,subQ4,subQ3,sQuery(id+"F0.wireOp",EDGE,"E39.0"),sQuery(id+"F0.wireOp",EDGE,"E40.0")])],"isStart":false})]}),makeQuery(id+"F7.opExtrude","CAP_FACE",FACE,{"disambiguationData":[OSD([subQ2,subQ1,subQ0,sQuery(id+"F0.wireOp",EDGE,"E48.0"),sQuery(id+"F0.wireOp",EDGE,"E49.0")])],"isStart":false})]});}
            extrude(context, id + "F8", {"entities" : qUnion([Q0, Q1]), "operationType" : NewBodyOperationType.ADD, "endBound" : BoundingType.UP_TO_SURFACE, "depth" : 12.7 * mm, "endBoundEntityFace" : qUnion([Q2]), "offsetDistance" : 25.4 * mm});
        }
        {
            var Q0;
            {var subQ0=sQuery(id+"F0.wireOp",EDGE,"E22");Q0=makeQuery(id+"F0.imprint","IMPRINT",FACE,{"disambiguationData":[TD([[makeQuery(id+"F0.imprint","IMPRINT",EDGE,{"derivedFrom":subQ0}),1.0]])]});}
            var Q1;
            {var subQ0=sQuery(id+"F0.wireOp",EDGE,"E18");var subQ1=sQuery(id+"F0.wireOp",EDGE,"E0.bottom");var subQ2=sQuery(id+"F0.wireOp",EDGE,"E16");var subQ3=sQuery(id+"F0.wireOp",EDGE,"E27.5");var subQ4=sQuery(id+"F0.wireOp",EDGE,"E27.4");var subQ5=sQuery(id+"F0.wireOp",EDGE,"E28.1");var subQ6=sQuery(id+"F0.wireOp",EDGE,"E28.0");var subQ7=sQuery(id+"F0.wireOp",EDGE,"E17");var subQ8=sQuery(id+"F0.wireOp",EDGE,"E28.3");var subQ9=sQuery(id+"F0.wireOp",EDGE,"E28.2");var subQ10=sQuery(id+"F0.wireOp",EDGE,"E27.1");var subQ11=sQuery(id+"F0.wireOp",EDGE,"E27.0");var subQ12=sQuery(id+"F0.wireOp",EDGE,"E27.3");var subQ13=sQuery(id+"F0.wireOp",EDGE,"E27.2");var subQ14=sQuery(id+"F0.wireOp",EDGE,"E2.bottom");var subQ15=sQuery(id+"F0.wireOp",EDGE,"E1.bottom");var subQ16=sQuery(id+"F0.wireOp",EDGE,"E15");var subQ17=sQuery(id+"F0.wireOp",EDGE,"E1.left");var subQ18=sQuery(id+"F0.wireOp",EDGE,"E2.left");Q1=makeQuery(id+"F8.boolean.opBoolean","MERGE",FACE,{"derivedFrom":[makeQuery(id+"F7.boolean.opBoolean","MERGE",FACE,{"derivedFrom":[makeQuery(id+"F6.boolean.opBoolean","MERGE",FACE,{"derivedFrom":[makeQuery(id+"F2.boolean.opBoolean","MERGE",FACE,{"derivedFrom":[makeQuery(id+"F1.opExtrude","CAP_FACE",FACE,{"disambiguationData":[OSD([subQ14,sQuery(id+"F0.wireOp",EDGE,"E2.top"),subQ18,sQuery(id+"F0.wireOp",EDGE,"E2.right")])],"isStart":false}),makeQuery(id+"F2.opExtrude","CAP_FACE",FACE,{"disambiguationData":[OSD([subQ1,subQ18,sQuery(id+"F0.wireOp",EDGE,"E53"),sQuery(id+"F0.wireOp",EDGE,"E59"),sQuery(id+"F0.wireOp",EDGE,"E60"),sQuery(id+"F0.wireOp",EDGE,"E61"),sQuery(id+"F0.wireOp",EDGE,"E63"),sQuery(id+"F0.wireOp",EDGE,"E65")])],"isStart":false})]}),makeQuery(id+"F5.boolean.opBoolean","MERGE",FACE,{"derivedFrom":[makeQuery(id+"F4.boolean.opBoolean","MERGE",FACE,{"derivedFrom":[makeQuery(id+"F2.boolean.opBoolean","MERGE",FACE,{"derivedFrom":[makeQuery(id+"F1.opExtrude","CAP_FACE",FACE,{"disambiguationData":[OSD([subQ15,sQuery(id+"F0.wireOp",EDGE,"E1.top"),subQ17,sQuery(id+"F0.wireOp",EDGE,"E1.right"),subQ16])],"isStart":false}),makeQuery(id+"F2.opExtrude","CAP_FACE",FACE,{"disambiguationData":[OSD([subQ1,subQ17,subQ16,sQuery(id+"F0.wireOp",EDGE,"E54"),sQuery(id+"F0.wireOp",EDGE,"E55"),sQuery(id+"F0.wireOp",EDGE,"E56"),sQuery(id+"F0.wireOp",EDGE,"E57"),sQuery(id+"F0.wireOp",EDGE,"E58"),sQuery(id+"F0.wireOp",EDGE,"E62"),sQuery(id+"F0.wireOp",EDGE,"E64")])],"isStart":false})]}),makeQuery(id+"F4.opExtrude","CAP_FACE",FACE,{"disambiguationData":[OSD([subQ1,subQ7,sQuery(id+"F0.wireOp",EDGE,"E20"),sQuery(id+"F0.wireOp",EDGE,"E22"),subQ11,subQ10,subQ13,subQ12,subQ4,subQ3,subQ6,subQ5,subQ9,subQ8])],"isStart":false})]}),makeQuery(id+"F5.opExtrude","CAP_FACE",FACE,{"disambiguationData":[OSD([subQ15,subQ14,subQ2,subQ7,subQ0,sQuery(id+"F0.wireOp",EDGE,"E29.0"),sQuery(id+"F0.wireOp",EDGE,"E30"),sQuery(id+"F0.wireOp",EDGE,"E31.0")])],"isStart":false})]}),makeQuery(id+"F6.opExtrude","CAP_FACE",FACE,{"disambiguationData":[OSD([subQ1,subQ13,subQ12,sQuery(id+"F0.wireOp",EDGE,"E41.0"),sQuery(id+"F0.wireOp",EDGE,"E42.0")])],"isStart":false}),makeQuery(id+"F6.opExtrude","CAP_FACE",FACE,{"disambiguationData":[OSD([subQ1,subQ11,subQ10,sQuery(id+"F0.wireOp",EDGE,"E43.0"),sQuery(id+"F0.wireOp",EDGE,"E44.0")])],"isStart":false}),makeQuery(id+"F6.opExtrude","CAP_FACE",FACE,{"disambiguationData":[OSD([subQ7,subQ9,subQ8,sQuery(id+"F0.wireOp",EDGE,"E37.0"),sQuery(id+"F0.wireOp",EDGE,"E38.0")])],"isStart":false}),makeQuery(id+"F6.opExtrude","CAP_FACE",FACE,{"disambiguationData":[OSD([subQ7,subQ6,subQ5,sQuery(id+"F0.wireOp",EDGE,"E39.0"),sQuery(id+"F0.wireOp",EDGE,"E40.0")])],"isStart":false})]}),makeQuery(id+"F7.opExtrude","CAP_FACE",FACE,{"disambiguationData":[OSD([subQ1,subQ4,subQ3,sQuery(id+"F0.wireOp",EDGE,"E48.0"),sQuery(id+"F0.wireOp",EDGE,"E49.0")])],"isStart":false})]}),makeQuery(id+"F8.opExtrude","CAP_FACE",FACE,{"disambiguationData":[OSD([subQ1,subQ2,sQuery(id+"F0.wireOp",EDGE,"E21"),sQuery(id+"F0.wireOp",EDGE,"E51.0")])],"isStart":false}),makeQuery(id+"F8.opExtrude","CAP_FACE",FACE,{"disambiguationData":[OSD([subQ1,subQ0,sQuery(id+"F0.wireOp",EDGE,"E19"),sQuery(id+"F0.wireOp",EDGE,"E50.0")])],"isStart":false})]});}
            extrude(context, id + "F9", {"entities" : qUnion([Q0]), "operationType" : NewBodyOperationType.ADD, "endBound" : BoundingType.UP_TO_SURFACE, "depth" : 12.7 * mm, "endBoundEntityFace" : qUnion([Q1]), "offsetDistance" : 25.4 * mm});
        }
        {
            var Q0;
            {var subQ0=sQuery(id+"F0.wireOp",EDGE,"E20");Q0=makeQuery(id+"F0.imprint","IMPRINT",FACE,{"disambiguationData":[TD([[makeQuery(id+"F0.imprint","IMPRINT",EDGE,{"derivedFrom":subQ0}),1.0]])]});}
            var Q1;
            {var subQ0=sQuery(id+"F0.wireOp",EDGE,"E22");var subQ1=sQuery(id+"F0.wireOp",EDGE,"E21");var subQ2=sQuery(id+"F0.wireOp",EDGE,"E16");var subQ3=sQuery(id+"F0.wireOp",EDGE,"E18");var subQ4=sQuery(id+"F0.wireOp",EDGE,"E0.bottom");var subQ5=sQuery(id+"F0.wireOp",EDGE,"E27.5");var subQ6=sQuery(id+"F0.wireOp",EDGE,"E27.4");var subQ7=sQuery(id+"F0.wireOp",EDGE,"E28.1");var subQ8=sQuery(id+"F0.wireOp",EDGE,"E28.0");var subQ9=sQuery(id+"F0.wireOp",EDGE,"E17");var subQ10=sQuery(id+"F0.wireOp",EDGE,"E28.3");var subQ11=sQuery(id+"F0.wireOp",EDGE,"E28.2");var subQ12=sQuery(id+"F0.wireOp",EDGE,"E27.1");var subQ13=sQuery(id+"F0.wireOp",EDGE,"E27.0");var subQ14=sQuery(id+"F0.wireOp",EDGE,"E27.3");var subQ15=sQuery(id+"F0.wireOp",EDGE,"E27.2");var subQ16=sQuery(id+"F0.wireOp",EDGE,"E2.bottom");var subQ17=sQuery(id+"F0.wireOp",EDGE,"E1.bottom");var subQ18=sQuery(id+"F0.wireOp",EDGE,"E15");var subQ19=sQuery(id+"F0.wireOp",EDGE,"E1.left");var subQ20=sQuery(id+"F0.wireOp",EDGE,"E2.left");Q1=makeQuery(id+"F9.boolean.opBoolean","MERGE",FACE,{"derivedFrom":[makeQuery(id+"F8.boolean.opBoolean","MERGE",FACE,{"derivedFrom":[makeQuery(id+"F7.boolean.opBoolean","MERGE",FACE,{"derivedFrom":[makeQuery(id+"F6.boolean.opBoolean","MERGE",FACE,{"derivedFrom":[makeQuery(id+"F2.boolean.opBoolean","MERGE",FACE,{"derivedFrom":[makeQuery(id+"F1.opExtrude","CAP_FACE",FACE,{"disambiguationData":[OSD([subQ16,sQuery(id+"F0.wireOp",EDGE,"E2.top"),subQ20,sQuery(id+"F0.wireOp",EDGE,"E2.right")])],"isStart":false}),makeQuery(id+"F2.opExtrude","CAP_FACE",FACE,{"disambiguationData":[OSD([subQ4,subQ20,sQuery(id+"F0.wireOp",EDGE,"E53"),sQuery(id+"F0.wireOp",EDGE,"E59"),sQuery(id+"F0.wireOp",EDGE,"E60"),sQuery(id+"F0.wireOp",EDGE,"E61"),sQuery(id+"F0.wireOp",EDGE,"E63"),sQuery(id+"F0.wireOp",EDGE,"E65")])],"isStart":false})]}),makeQuery(id+"F5.boolean.opBoolean","MERGE",FACE,{"derivedFrom":[makeQuery(id+"F4.boolean.opBoolean","MERGE",FACE,{"derivedFrom":[makeQuery(id+"F2.boolean.opBoolean","MERGE",FACE,{"derivedFrom":[makeQuery(id+"F1.opExtrude","CAP_FACE",FACE,{"disambiguationData":[OSD([subQ17,sQuery(id+"F0.wireOp",EDGE,"E1.top"),subQ19,sQuery(id+"F0.wireOp",EDGE,"E1.right"),subQ18])],"isStart":false}),makeQuery(id+"F2.opExtrude","CAP_FACE",FACE,{"disambiguationData":[OSD([subQ4,subQ19,subQ18,sQuery(id+"F0.wireOp",EDGE,"E54"),sQuery(id+"F0.wireOp",EDGE,"E55"),sQuery(id+"F0.wireOp",EDGE,"E56"),sQuery(id+"F0.wireOp",EDGE,"E57"),sQuery(id+"F0.wireOp",EDGE,"E58"),sQuery(id+"F0.wireOp",EDGE,"E62"),sQuery(id+"F0.wireOp",EDGE,"E64")])],"isStart":false})]}),makeQuery(id+"F4.opExtrude","CAP_FACE",FACE,{"disambiguationData":[OSD([subQ4,subQ9,sQuery(id+"F0.wireOp",EDGE,"E20"),subQ0,subQ13,subQ12,subQ15,subQ14,subQ6,subQ5,subQ8,subQ7,subQ11,subQ10])],"isStart":false})]}),makeQuery(id+"F5.opExtrude","CAP_FACE",FACE,{"disambiguationData":[OSD([subQ17,subQ16,subQ2,subQ9,subQ3,sQuery(id+"F0.wireOp",EDGE,"E29.0"),sQuery(id+"F0.wireOp",EDGE,"E30"),sQuery(id+"F0.wireOp",EDGE,"E31.0")])],"isStart":false})]}),makeQuery(id+"F6.opExtrude","CAP_FACE",FACE,{"disambiguationData":[OSD([subQ4,subQ15,subQ14,sQuery(id+"F0.wireOp",EDGE,"E41.0"),sQuery(id+"F0.wireOp",EDGE,"E42.0")])],"isStart":false}),makeQuery(id+"F6.opExtrude","CAP_FACE",FACE,{"disambiguationData":[OSD([subQ4,subQ13,subQ12,sQuery(id+"F0.wireOp",EDGE,"E43.0"),sQuery(id+"F0.wireOp",EDGE,"E44.0")])],"isStart":false}),makeQuery(id+"F6.opExtrude","CAP_FACE",FACE,{"disambiguationData":[OSD([subQ9,subQ11,subQ10,sQuery(id+"F0.wireOp",EDGE,"E37.0"),sQuery(id+"F0.wireOp",EDGE,"E38.0")])],"isStart":false}),makeQuery(id+"F6.opExtrude","CAP_FACE",FACE,{"disambiguationData":[OSD([subQ9,subQ8,subQ7,sQuery(id+"F0.wireOp",EDGE,"E39.0"),sQuery(id+"F0.wireOp",EDGE,"E40.0")])],"isStart":false})]}),makeQuery(id+"F7.opExtrude","CAP_FACE",FACE,{"disambiguationData":[OSD([subQ4,subQ6,subQ5,sQuery(id+"F0.wireOp",EDGE,"E48.0"),sQuery(id+"F0.wireOp",EDGE,"E49.0")])],"isStart":false})]}),makeQuery(id+"F8.opExtrude","CAP_FACE",FACE,{"disambiguationData":[OSD([subQ4,subQ2,subQ1,sQuery(id+"F0.wireOp",EDGE,"E51.0")])],"isStart":false}),makeQuery(id+"F8.opExtrude","CAP_FACE",FACE,{"disambiguationData":[OSD([subQ4,subQ3,sQuery(id+"F0.wireOp",EDGE,"E19"),sQuery(id+"F0.wireOp",EDGE,"E50.0")])],"isStart":false})]}),makeQuery(id+"F9.opExtrude","CAP_FACE",FACE,{"disambiguationData":[OSD([subQ2,subQ1,subQ0,sQuery(id+"F0.wireOp",EDGE,"E52.0")])],"isStart":false})]});}
            extrude(context, id + "F10", {"entities" : qUnion([Q0]), "operationType" : NewBodyOperationType.ADD, "endBound" : BoundingType.UP_TO_SURFACE, "depth" : 25.4 * mm, "endBoundEntityFace" : qUnion([Q1]), "offsetDistance" : 25.4 * mm});
        }
        {
            var Q0;
            {var subQ7=sQuery(id+"F0.wireOp",EDGE,"E70.0");Q0=makeQuery(id+"F0.imprint","IMPRINT",FACE,{"disambiguationData":[TD([[makeQuery(id+"F0.imprint","IMPRINT",EDGE,{"derivedFrom":subQ7}),1.0]])]});}
            var Q1;
            {var subQ0=sQuery(id+"F0.wireOp",EDGE,"E20");var subQ1=sQuery(id+"F0.wireOp",EDGE,"E19");var subQ2=sQuery(id+"F0.wireOp",EDGE,"E18");var subQ3=sQuery(id+"F0.wireOp",EDGE,"E22");var subQ4=sQuery(id+"F0.wireOp",EDGE,"E21");var subQ5=sQuery(id+"F0.wireOp",EDGE,"E16");var subQ6=sQuery(id+"F0.wireOp",EDGE,"E0.bottom");var subQ7=sQuery(id+"F0.wireOp",EDGE,"E27.5");var subQ8=sQuery(id+"F0.wireOp",EDGE,"E27.4");var subQ9=sQuery(id+"F0.wireOp",EDGE,"E28.1");var subQ10=sQuery(id+"F0.wireOp",EDGE,"E28.0");var subQ11=sQuery(id+"F0.wireOp",EDGE,"E17");var subQ12=sQuery(id+"F0.wireOp",EDGE,"E28.3");var subQ13=sQuery(id+"F0.wireOp",EDGE,"E28.2");var subQ14=sQuery(id+"F0.wireOp",EDGE,"E27.1");var subQ15=sQuery(id+"F0.wireOp",EDGE,"E27.0");var subQ16=sQuery(id+"F0.wireOp",EDGE,"E27.3");var subQ17=sQuery(id+"F0.wireOp",EDGE,"E27.2");var subQ18=sQuery(id+"F0.wireOp",EDGE,"E2.bottom");var subQ19=sQuery(id+"F0.wireOp",EDGE,"E1.bottom");var subQ20=sQuery(id+"F0.wireOp",EDGE,"E15");var subQ21=sQuery(id+"F0.wireOp",EDGE,"E1.left");var subQ22=sQuery(id+"F0.wireOp",EDGE,"E2.left");Q1=makeQuery(id+"F10.boolean.opBoolean","MERGE",FACE,{"derivedFrom":[makeQuery(id+"F9.boolean.opBoolean","MERGE",FACE,{"derivedFrom":[makeQuery(id+"F8.boolean.opBoolean","MERGE",FACE,{"derivedFrom":[makeQuery(id+"F7.boolean.opBoolean","MERGE",FACE,{"derivedFrom":[makeQuery(id+"F6.boolean.opBoolean","MERGE",FACE,{"derivedFrom":[makeQuery(id+"F2.boolean.opBoolean","MERGE",FACE,{"derivedFrom":[makeQuery(id+"F1.opExtrude","CAP_FACE",FACE,{"disambiguationData":[OSD([subQ18,sQuery(id+"F0.wireOp",EDGE,"E2.top"),subQ22,sQuery(id+"F0.wireOp",EDGE,"E2.right")])],"isStart":false}),makeQuery(id+"F2.opExtrude","CAP_FACE",FACE,{"disambiguationData":[OSD([subQ6,subQ22,sQuery(id+"F0.wireOp",EDGE,"E53"),sQuery(id+"F0.wireOp",EDGE,"E59"),sQuery(id+"F0.wireOp",EDGE,"E60"),sQuery(id+"F0.wireOp",EDGE,"E61"),sQuery(id+"F0.wireOp",EDGE,"E63"),sQuery(id+"F0.wireOp",EDGE,"E65")])],"isStart":false})]}),makeQuery(id+"F5.boolean.opBoolean","MERGE",FACE,{"derivedFrom":[makeQuery(id+"F4.boolean.opBoolean","MERGE",FACE,{"derivedFrom":[makeQuery(id+"F2.boolean.opBoolean","MERGE",FACE,{"derivedFrom":[makeQuery(id+"F1.opExtrude","CAP_FACE",FACE,{"disambiguationData":[OSD([subQ19,sQuery(id+"F0.wireOp",EDGE,"E1.top"),subQ21,sQuery(id+"F0.wireOp",EDGE,"E1.right"),subQ20])],"isStart":false}),makeQuery(id+"F2.opExtrude","CAP_FACE",FACE,{"disambiguationData":[OSD([subQ6,subQ21,subQ20,sQuery(id+"F0.wireOp",EDGE,"E54"),sQuery(id+"F0.wireOp",EDGE,"E55"),sQuery(id+"F0.wireOp",EDGE,"E56"),sQuery(id+"F0.wireOp",EDGE,"E57"),sQuery(id+"F0.wireOp",EDGE,"E58"),sQuery(id+"F0.wireOp",EDGE,"E62"),sQuery(id+"F0.wireOp",EDGE,"E64")])],"isStart":false})]}),makeQuery(id+"F4.opExtrude","CAP_FACE",FACE,{"disambiguationData":[OSD([subQ6,subQ11,subQ0,subQ3,subQ15,subQ14,subQ17,subQ16,subQ8,subQ7,subQ10,subQ9,subQ13,subQ12])],"isStart":false})]}),makeQuery(id+"F5.opExtrude","CAP_FACE",FACE,{"disambiguationData":[OSD([subQ19,subQ18,subQ5,subQ11,subQ2,sQuery(id+"F0.wireOp",EDGE,"E29.0"),sQuery(id+"F0.wireOp",EDGE,"E30"),sQuery(id+"F0.wireOp",EDGE,"E31.0")])],"isStart":false})]}),makeQuery(id+"F6.opExtrude","CAP_FACE",FACE,{"disambiguationData":[OSD([subQ6,subQ17,subQ16,sQuery(id+"F0.wireOp",EDGE,"E41.0"),sQuery(id+"F0.wireOp",EDGE,"E42.0")])],"isStart":false}),makeQuery(id+"F6.opExtrude","CAP_FACE",FACE,{"disambiguationData":[OSD([subQ6,subQ15,subQ14,sQuery(id+"F0.wireOp",EDGE,"E43.0"),sQuery(id+"F0.wireOp",EDGE,"E44.0")])],"isStart":false}),makeQuery(id+"F6.opExtrude","CAP_FACE",FACE,{"disambiguationData":[OSD([subQ11,subQ13,subQ12,sQuery(id+"F0.wireOp",EDGE,"E37.0"),sQuery(id+"F0.wireOp",EDGE,"E38.0")])],"isStart":false}),makeQuery(id+"F6.opExtrude","CAP_FACE",FACE,{"disambiguationData":[OSD([subQ11,subQ10,subQ9,sQuery(id+"F0.wireOp",EDGE,"E39.0"),sQuery(id+"F0.wireOp",EDGE,"E40.0")])],"isStart":false})]}),makeQuery(id+"F7.opExtrude","CAP_FACE",FACE,{"disambiguationData":[OSD([subQ6,subQ8,subQ7,sQuery(id+"F0.wireOp",EDGE,"E48.0"),sQuery(id+"F0.wireOp",EDGE,"E49.0")])],"isStart":false})]}),makeQuery(id+"F8.opExtrude","CAP_FACE",FACE,{"disambiguationData":[OSD([subQ6,subQ5,subQ4,sQuery(id+"F0.wireOp",EDGE,"E51.0")])],"isStart":false}),makeQuery(id+"F8.opExtrude","CAP_FACE",FACE,{"disambiguationData":[OSD([subQ6,subQ2,subQ1,sQuery(id+"F0.wireOp",EDGE,"E50.0")])],"isStart":false})]}),makeQuery(id+"F9.opExtrude","CAP_FACE",FACE,{"disambiguationData":[OSD([subQ5,subQ4,subQ3,sQuery(id+"F0.wireOp",EDGE,"E52.0")])],"isStart":false})]}),makeQuery(id+"F10.opExtrude","CAP_FACE",FACE,{"disambiguationData":[OSD([subQ2,subQ1,subQ0,sQuery(id+"F0.wireOp",EDGE,"E66.0")])],"isStart":false})]});}
            extrude(context, id + "F11", {"entities" : qUnion([Q0]), "operationType" : NewBodyOperationType.ADD, "endBound" : BoundingType.UP_TO_SURFACE, "depth" : 25.4 * mm, "endBoundEntityFace" : qUnion([Q1]), "offsetDistance" : 25.4 * mm});
        }
        {
            var Q0;
            {var subQ28=sQuery(id+"F0.wireOp",EDGE,"E29.0");Q0=makeQuery(id+"F0.imprint","IMPRINT",FACE,{"disambiguationData":[TD([[makeQuery(id+"F0.imprint","IMPRINT",EDGE,{"derivedFrom":subQ28}),1.0]])]});}
            var sketch = newSketch(context, id + "F12", { "sketchPlane" : qUnion([Q0])});
            skLineSegment(sketch, "E84.bottom", {"start": v(43.97, 27.89) * mm, "end": v(42.1, 27.89) * mm});
            skLineSegment(sketch, "E84.top", {"start": v(43.97, 24.3) * mm, "end": v(42.1, 24.3) * mm});
            skLineSegment(sketch, "E84.left", {"start": v(43.97, 27.89) * mm, "end": v(43.97, 24.3) * mm});
            skLineSegment(sketch, "E84.right", {"start": v(42.1, 27.89) * mm, "end": v(42.1, 24.3) * mm});
            skLineSegment(sketch, "E85.bottom", {"start": v(23.77, 24.3) * mm, "end": v(21.23, 24.3) * mm});
            skLineSegment(sketch, "E85.top", {"start": v(23.77, 27.89) * mm, "end": v(21.23, 27.89) * mm});
            skLineSegment(sketch, "E85.left", {"start": v(23.77, 24.3) * mm, "end": v(23.77, 27.89) * mm});
            skLineSegment(sketch, "E85.right", {"start": v(21.23, 24.3) * mm, "end": v(21.23, 27.89) * mm});
            skLineSegment(sketch, "E86.bottom", {"start": v(1.93, 27.89) * mm, "end": v(-1.93, 27.89) * mm});
            skLineSegment(sketch, "E86.top", {"start": v(1.93, 24.3) * mm, "end": v(-1.93, 24.3) * mm});
            skLineSegment(sketch, "E86.left", {"start": v(1.93, 27.89) * mm, "end": v(1.93, 24.3) * mm});
            skLineSegment(sketch, "E86.right", {"start": v(-1.93, 27.89) * mm, "end": v(-1.93, 24.3) * mm});
            skLineSegment(sketch, "E87.bottom", {"start": v(-21.23, 27.89) * mm, "end": v(-23.77, 27.89) * mm});
            skLineSegment(sketch, "E87.top", {"start": v(-21.23, 24.3) * mm, "end": v(-23.77, 24.3) * mm});
            skLineSegment(sketch, "E87.left", {"start": v(-21.23, 27.89) * mm, "end": v(-21.23, 24.3) * mm});
            skLineSegment(sketch, "E87.right", {"start": v(-23.77, 27.89) * mm, "end": v(-23.77, 24.3) * mm});
            skLineSegment(sketch, "E88.bottom", {"start": v(-42.1, 27.89) * mm, "end": v(-43.97, 27.89) * mm});
            skLineSegment(sketch, "E88.top", {"start": v(-42.1, 24.3) * mm, "end": v(-43.97, 24.3) * mm});
            skLineSegment(sketch, "E88.left", {"start": v(-42.1, 27.89) * mm, "end": v(-42.1, 24.3) * mm});
            skLineSegment(sketch, "E88.right", {"start": v(-43.97, 27.89) * mm, "end": v(-43.97, 24.3) * mm});
            skSolve(sketch);
        }
        {
            var Q0;
            {var subQ0=sQuery(id+"F0.wireOp",EDGE,"E0.bottom");var subQ1=makeQuery(id+"F0.imprint","INTERSECT",VERTEX,{"derivedFrom":[subQ0,sQuery(id+"F0.wireOp",EDGE,"E41.0")]});var subQ3=makeQuery(id+"F0.imprint","INTERSECT",VERTEX,{"derivedFrom":[subQ0,sQuery(id+"F0.wireOp",EDGE,"E42.0")]});var subQ5=makeQuery(id+"F0.imprint","INTERSECT",VERTEX,{"derivedFrom":[subQ0,sQuery(id+"F0.wireOp",EDGE,"E27.2")]});var subQ7=makeQuery(id+"F0.imprint","INTERSECT",VERTEX,{"derivedFrom":[subQ0,sQuery(id+"F0.wireOp",EDGE,"E27.3")]});var subQ8=makeQuery(id+"F0.imprint","INTERSECT",VERTEX,{"derivedFrom":[subQ0,sQuery(id+"F0.wireOp",EDGE,"E27.4")]});var subQ9=makeQuery(id+"F0.imprint","INTERSECT",VERTEX,{"derivedFrom":[subQ0,sQuery(id+"F0.wireOp",EDGE,"E50.0")]});var subQ10=sQuery(id+"F0.wireOp",EDGE,"E1.bottom");var subQ11=makeQuery(id+"F0.imprint","INTERSECT",VERTEX,{"derivedFrom":[subQ0,sQuery(id+"F0.wireOp",EDGE,"E49.0")]});var subQ12=makeQuery(id+"F0.imprint","INTERSECT",VERTEX,{"derivedFrom":[subQ0,sQuery(id+"F0.wireOp",EDGE,"E65")]});var subQ14=makeQuery(id+"F0.imprint","INTERSECT",VERTEX,{"derivedFrom":[subQ0,sQuery(id+"F0.wireOp",EDGE,"E43.0")]});var subQ15=makeQuery(id+"F0.imprint","INTERSECT",VERTEX,{"derivedFrom":[subQ0,sQuery(id+"F0.wireOp",EDGE,"E44.0")]});var subQ17=makeQuery(id+"F0.imprint","INTERSECT",VERTEX,{"derivedFrom":[subQ0,sQuery(id+"F0.wireOp",EDGE,"E27.0")]});var subQ19=makeQuery(id+"F0.imprint","INTERSECT",VERTEX,{"derivedFrom":[subQ0,sQuery(id+"F0.wireOp",EDGE,"E27.1")]});var subQ20=makeQuery(id+"F0.imprint","INTERSECT",VERTEX,{"derivedFrom":[subQ0,sQuery(id+"F0.wireOp",EDGE,"E27.5")]});var subQ21=makeQuery(id+"F0.imprint","INTERSECT",VERTEX,{"derivedFrom":[subQ0,sQuery(id+"F0.wireOp",EDGE,"E51.0")]});var subQ22=sQuery(id+"F0.wireOp",EDGE,"E2.bottom");Q0=qUnion([makeQuery(id+"F3.boolean.opBoolean","MERGE",FACE,{"derivedFrom":[makeQuery(id+"F2.boolean.opBoolean","MERGE",FACE,{"derivedFrom":[makeQuery(id+"F1.opExtrude","SWEPT_FACE",FACE,{"disambiguationData":[OSD([subQ22])]}),makeQuery(id+"F2.opExtrude","SWEPT_FACE",FACE,{"disambiguationData":[OSD([subQ0]),TDD([makeQuery(id+"F0.imprint","IMPRINT",EDGE,{"disambiguationData":[TD([[subQ14,1.0]])],"derivedFrom":subQ0}),makeQuery(id+"F0.imprint","IMPRINT",EDGE,{"disambiguationData":[TD([[subQ12,-1.0]])],"derivedFrom":subQ0}),makeQuery(id+"F0.imprint","IMPRINT",EDGE,{"disambiguationData":[TD([[subQ15,-1.0]])],"derivedFrom":subQ0}),makeQuery(id+"F0.imprint","IMPRINT",EDGE,{"disambiguationData":[TD([[subQ21,-1.0]])],"derivedFrom":subQ0}),makeQuery(id+"F0.imprint","IMPRINT",EDGE,{"disambiguationData":[TD([[subQ21,1.0]])],"derivedFrom":subQ0}),makeQuery(id+"F0.imprint","IMPRINT",EDGE,{"disambiguationData":[TD([[subQ20,-1.0]])],"derivedFrom":subQ0}),makeQuery(id+"F0.imprint","IMPRINT",EDGE,{"disambiguationData":[TD([[subQ19,1.0]])],"derivedFrom":subQ0}),makeQuery(id+"F0.imprint","IMPRINT",EDGE,{"disambiguationData":[TD([[subQ17,-1.0]])],"derivedFrom":subQ0}),makeQuery(id+"F0.imprint","IMPRINT",EDGE,{"disambiguationData":[TD([[subQ15,1.0]])],"derivedFrom":subQ0}),makeQuery(id+"F0.imprint","IMPRINT",EDGE,{"disambiguationData":[TD([[subQ14,-1.0]])],"derivedFrom":subQ0})])]})]}),makeQuery(id+"F3.opExtrude","SWEPT_FACE",FACE,{"disambiguationData":[OSD([subQ0]),TDD([makeQuery(id+"F0.imprint","IMPRINT",EDGE,{"disambiguationData":[TD([[subQ12,1.0]])],"derivedFrom":subQ0}),makeQuery(id+"F0.imprint","IMPRINT",EDGE,{"disambiguationData":[TD([[subQ11,1.0]])],"derivedFrom":subQ0})])]})]}),makeQuery(id+"F2.boolean.opBoolean","MERGE",FACE,{"derivedFrom":[makeQuery(id+"F1.opExtrude","SWEPT_FACE",FACE,{"disambiguationData":[OSD([subQ10])]}),makeQuery(id+"F2.opExtrude","SWEPT_FACE",FACE,{"disambiguationData":[OSD([subQ0]),TDD([makeQuery(id+"F0.imprint","IMPRINT",EDGE,{"disambiguationData":[TD([[subQ1,-1.0]])],"derivedFrom":subQ0}),makeQuery(id+"F0.imprint","IMPRINT",EDGE,{"disambiguationData":[TD([[subQ8,-1.0]])],"derivedFrom":subQ0}),makeQuery(id+"F0.imprint","IMPRINT",EDGE,{"disambiguationData":[TD([[subQ5,-1.0]])],"derivedFrom":subQ0}),makeQuery(id+"F0.imprint","IMPRINT",EDGE,{"disambiguationData":[TD([[subQ9,1.0]])],"derivedFrom":subQ0}),makeQuery(id+"F0.imprint","IMPRINT",EDGE,{"disambiguationData":[TD([[subQ9,-1.0]])],"derivedFrom":subQ0}),makeQuery(id+"F0.imprint","IMPRINT",EDGE,{"disambiguationData":[TD([[subQ8,1.0]])],"derivedFrom":subQ0}),makeQuery(id+"F0.imprint","IMPRINT",EDGE,{"disambiguationData":[TD([[subQ7,-1.0]])],"derivedFrom":subQ0}),makeQuery(id+"F0.imprint","IMPRINT",EDGE,{"disambiguationData":[TD([[subQ5,1.0]])],"derivedFrom":subQ0}),makeQuery(id+"F0.imprint","IMPRINT",EDGE,{"disambiguationData":[TD([[subQ3,-1.0]])],"derivedFrom":subQ0}),makeQuery(id+"F0.imprint","IMPRINT",EDGE,{"disambiguationData":[TD([[subQ1,1.0]])],"derivedFrom":subQ0})])]})]})]);}
            var sketch = newSketch(context, id + "F13", { "sketchPlane" : qUnion([Q0])});
            skLineSegment(sketch, "E89.bottom", {"start": v(-7.62, 17.14) * mm, "end": v(7.62, 17.14) * mm});
            skLineSegment(sketch, "E89.top", {"start": v(-7.62, 1.9) * mm, "end": v(7.62, 1.9) * mm});
            skLineSegment(sketch, "E89.left", {"start": v(-7.62, 17.14) * mm, "end": v(-7.62, 1.9) * mm});
            skLineSegment(sketch, "E89.right", {"start": v(7.62, 17.14) * mm, "end": v(7.62, 1.9) * mm});
            skPoint(sketch, "E90", {"position": v(7.62, 9.53) * mm});
            skSolve(sketch);
        }
        {
            var Q0;
            {var subQ0=sQuery(id+"F0.wireOp",EDGE,"E2.left");var subQ1=sQuery(id+"F0.wireOp",EDGE,"E2.bottom");var subQ12=sQuery(id+"F0.wireOp",EDGE,"E65");var subQ15=sQuery(id+"F0.wireOp",EDGE,"E2.top");Q0=makeQuery(id+"FNRWj5r8XRpMM9b_2.opPattern","COPY",FACE,{"derivedFrom":makeQuery(id+"F3.boolean.opBoolean","SPLIT",FACE,{"disambiguationData":[TD([makeQuery(id+"F1.opExtrude","CAP_FACE",FACE,{"disambiguationData":[OSD([subQ1,subQ15,subQ0,sQuery(id+"F0.wireOp",EDGE,"E2.right")])],"isStart":false})])],"derivedFrom":makeQuery(id+"F2.opExtrude","SWEPT_FACE",FACE,{"disambiguationData":[OSD([subQ12])]})}),"instanceName":"1"});}
            var Q1;
            {var subQ10=sQuery(id+"F0.wireOp",EDGE,"E2.left");var subQ11=sQuery(id+"F0.wireOp",EDGE,"E2.bottom");var subQ12=sQuery(id+"F0.wireOp",EDGE,"E65");var subQ17=sQuery(id+"F0.wireOp",EDGE,"E2.top");Q1=makeQuery(id+"F3.boolean.opBoolean","SPLIT",FACE,{"disambiguationData":[TD([makeQuery(id+"F1.opExtrude","CAP_FACE",FACE,{"disambiguationData":[OSD([subQ11,subQ17,subQ10,sQuery(id+"F0.wireOp",EDGE,"E2.right")])],"isStart":false})])],"derivedFrom":makeQuery(id+"F2.opExtrude","SWEPT_FACE",FACE,{"disambiguationData":[OSD([subQ12])]})});}
            extrude(context, id + "F14", {"entities" : qUnion([Q0, Q1]), "operationType" : NewBodyOperationType.ADD, "endBound" : BoundingType.UP_TO_NEXT, "depth" : 25.4 * mm, "offsetDistance" : 25.4 * mm});
        }
        {
            var Q0;
            Q0=makeQuery(id+"F3.opExtrude","SWEPT_FACE",FACE,{"disambiguationData":[OSD([sQuery(id+"F0.wireOp",EDGE,"E11")])]});
            extrude(context, id + "F15", {"entities" : qUnion([Q0]), "operationType" : NewBodyOperationType.ADD, "endBound" : BoundingType.UP_TO_NEXT, "depth" : 25.4 * mm, "offsetDistance" : 25.4 * mm});
        }
        {
            var Q0;
            {var subQ2=sQuery(id+"F0.wireOp",EDGE,"E72");Q0=makeQuery(id+"F0.imprint","IMPRINT",FACE,{"disambiguationData":[TD([[makeQuery(id+"F0.imprint","IMPRINT",EDGE,{"derivedFrom":subQ2}),-1.0]])]});}
            var Q1;
            {var subQ0=sQuery(id+"F0.wireOp",EDGE,"E71");Q1=makeQuery(id+"F0.imprint","IMPRINT",FACE,{"disambiguationData":[TD([[makeQuery(id+"F0.imprint","IMPRINT",EDGE,{"derivedFrom":subQ0}),-1.0]])]});}
            var Q2;
            {var subQ2=sQuery(id+"F0.wireOp",EDGE,"E74");Q2=makeQuery(id+"F0.imprint","IMPRINT",FACE,{"disambiguationData":[TD([[makeQuery(id+"F0.imprint","IMPRINT",EDGE,{"derivedFrom":subQ2}),-1.0]])]});}
            var Q3;
            {var subQ2=sQuery(id+"F0.wireOp",EDGE,"E73");Q3=makeQuery(id+"F0.imprint","IMPRINT",FACE,{"disambiguationData":[TD([[makeQuery(id+"F0.imprint","IMPRINT",EDGE,{"derivedFrom":subQ2}),-1.0]])]});}
            var Q4;
            {var subQ0=sQuery(id+"F0.wireOp",EDGE,"E65");var subQ1=sQuery(id+"F0.wireOp",EDGE,"E60");var subQ2=sQuery(id+"F0.wireOp",EDGE,"E55");var subQ3=sQuery(id+"F0.wireOp",EDGE,"E20");var subQ4=sQuery(id+"F0.wireOp",EDGE,"E19");var subQ5=sQuery(id+"F0.wireOp",EDGE,"E18");var subQ6=sQuery(id+"F0.wireOp",EDGE,"E22");var subQ7=sQuery(id+"F0.wireOp",EDGE,"E21");var subQ8=sQuery(id+"F0.wireOp",EDGE,"E16");var subQ9=sQuery(id+"F0.wireOp",EDGE,"E0.bottom");var subQ10=sQuery(id+"F0.wireOp",EDGE,"E27.5");var subQ11=sQuery(id+"F0.wireOp",EDGE,"E27.4");var subQ12=sQuery(id+"F0.wireOp",EDGE,"E28.1");var subQ13=sQuery(id+"F0.wireOp",EDGE,"E28.0");var subQ14=sQuery(id+"F0.wireOp",EDGE,"E17");var subQ15=sQuery(id+"F0.wireOp",EDGE,"E28.3");var subQ16=sQuery(id+"F0.wireOp",EDGE,"E28.2");var subQ17=sQuery(id+"F0.wireOp",EDGE,"E27.1");var subQ18=sQuery(id+"F0.wireOp",EDGE,"E27.0");var subQ19=sQuery(id+"F0.wireOp",EDGE,"E27.3");var subQ20=sQuery(id+"F0.wireOp",EDGE,"E27.2");var subQ21=sQuery(id+"F0.wireOp",EDGE,"E2.bottom");var subQ22=sQuery(id+"F0.wireOp",EDGE,"E1.bottom");var subQ23=sQuery(id+"F0.wireOp",EDGE,"E15");var subQ24=sQuery(id+"F0.wireOp",EDGE,"E1.left");var subQ25=sQuery(id+"F0.wireOp",EDGE,"E2.left");Q4=makeQuery(id+"F14.boolean.opBoolean","MERGE",FACE,{"derivedFrom":[makeQuery(id+"F11.boolean.opBoolean","MERGE",FACE,{"derivedFrom":[makeQuery(id+"F10.boolean.opBoolean","MERGE",FACE,{"derivedFrom":[makeQuery(id+"F9.boolean.opBoolean","MERGE",FACE,{"derivedFrom":[makeQuery(id+"F8.boolean.opBoolean","MERGE",FACE,{"derivedFrom":[makeQuery(id+"F7.boolean.opBoolean","MERGE",FACE,{"derivedFrom":[makeQuery(id+"F6.boolean.opBoolean","MERGE",FACE,{"derivedFrom":[makeQuery(id+"F2.boolean.opBoolean","MERGE",FACE,{"derivedFrom":[makeQuery(id+"F1.opExtrude","CAP_FACE",FACE,{"disambiguationData":[OSD([subQ21,sQuery(id+"F0.wireOp",EDGE,"E2.top"),subQ25,sQuery(id+"F0.wireOp",EDGE,"E2.right")])],"isStart":false}),makeQuery(id+"F2.opExtrude","CAP_FACE",FACE,{"disambiguationData":[OSD([subQ9,subQ25,sQuery(id+"F0.wireOp",EDGE,"E53"),sQuery(id+"F0.wireOp",EDGE,"E59"),subQ1,sQuery(id+"F0.wireOp",EDGE,"E61"),sQuery(id+"F0.wireOp",EDGE,"E63"),subQ0])],"isStart":false})]}),makeQuery(id+"F5.boolean.opBoolean","MERGE",FACE,{"derivedFrom":[makeQuery(id+"F4.boolean.opBoolean","MERGE",FACE,{"derivedFrom":[makeQuery(id+"F2.boolean.opBoolean","MERGE",FACE,{"derivedFrom":[makeQuery(id+"F1.opExtrude","CAP_FACE",FACE,{"disambiguationData":[OSD([subQ22,sQuery(id+"F0.wireOp",EDGE,"E1.top"),subQ24,sQuery(id+"F0.wireOp",EDGE,"E1.right"),subQ23])],"isStart":false}),makeQuery(id+"F2.opExtrude","CAP_FACE",FACE,{"disambiguationData":[OSD([subQ9,subQ24,subQ23,sQuery(id+"F0.wireOp",EDGE,"E54"),subQ2,sQuery(id+"F0.wireOp",EDGE,"E56"),sQuery(id+"F0.wireOp",EDGE,"E57"),sQuery(id+"F0.wireOp",EDGE,"E58"),sQuery(id+"F0.wireOp",EDGE,"E62"),sQuery(id+"F0.wireOp",EDGE,"E64")])],"isStart":false})]}),makeQuery(id+"F4.opExtrude","CAP_FACE",FACE,{"disambiguationData":[OSD([subQ9,subQ14,subQ3,subQ6,subQ18,subQ17,subQ20,subQ19,subQ11,subQ10,subQ13,subQ12,subQ16,subQ15])],"isStart":false})]}),makeQuery(id+"F5.opExtrude","CAP_FACE",FACE,{"disambiguationData":[OSD([subQ22,subQ21,subQ8,subQ14,subQ5,sQuery(id+"F0.wireOp",EDGE,"E29.0"),sQuery(id+"F0.wireOp",EDGE,"E30"),sQuery(id+"F0.wireOp",EDGE,"E31.0")])],"isStart":false})]}),makeQuery(id+"F6.opExtrude","CAP_FACE",FACE,{"disambiguationData":[OSD([subQ9,subQ20,subQ19,sQuery(id+"F0.wireOp",EDGE,"E41.0"),sQuery(id+"F0.wireOp",EDGE,"E42.0")])],"isStart":false}),makeQuery(id+"F6.opExtrude","CAP_FACE",FACE,{"disambiguationData":[OSD([subQ9,subQ18,subQ17,sQuery(id+"F0.wireOp",EDGE,"E43.0"),sQuery(id+"F0.wireOp",EDGE,"E44.0")])],"isStart":false}),makeQuery(id+"F6.opExtrude","CAP_FACE",FACE,{"disambiguationData":[OSD([subQ14,subQ16,subQ15,sQuery(id+"F0.wireOp",EDGE,"E37.0"),sQuery(id+"F0.wireOp",EDGE,"E38.0")])],"isStart":false}),makeQuery(id+"F6.opExtrude","CAP_FACE",FACE,{"disambiguationData":[OSD([subQ14,subQ13,subQ12,sQuery(id+"F0.wireOp",EDGE,"E39.0"),sQuery(id+"F0.wireOp",EDGE,"E40.0")])],"isStart":false})]}),makeQuery(id+"F7.opExtrude","CAP_FACE",FACE,{"disambiguationData":[OSD([subQ9,subQ11,subQ10,sQuery(id+"F0.wireOp",EDGE,"E48.0"),sQuery(id+"F0.wireOp",EDGE,"E49.0")])],"isStart":false})]}),makeQuery(id+"F8.opExtrude","CAP_FACE",FACE,{"disambiguationData":[OSD([subQ9,subQ8,subQ7,sQuery(id+"F0.wireOp",EDGE,"E51.0")])],"isStart":false}),makeQuery(id+"F8.opExtrude","CAP_FACE",FACE,{"disambiguationData":[OSD([subQ9,subQ5,subQ4,sQuery(id+"F0.wireOp",EDGE,"E50.0")])],"isStart":false})]}),makeQuery(id+"F9.opExtrude","CAP_FACE",FACE,{"disambiguationData":[OSD([subQ8,subQ7,subQ6,sQuery(id+"F0.wireOp",EDGE,"E52.0")])],"isStart":false})]}),makeQuery(id+"F10.opExtrude","CAP_FACE",FACE,{"disambiguationData":[OSD([subQ5,subQ4,subQ3,sQuery(id+"F0.wireOp",EDGE,"E66.0")])],"isStart":false})]}),makeQuery(id+"F11.opExtrude","CAP_FACE",FACE,{"disambiguationData":[OSD([subQ2,subQ1,sQuery(id+"F0.wireOp",EDGE,"E67"),sQuery(id+"F0.wireOp",EDGE,"E68"),sQuery(id+"F0.wireOp",EDGE,"E69"),sQuery(id+"F0.wireOp",EDGE,"E70.0"),sQuery(id+"F0.wireOp",EDGE,"E70.1"),sQuery(id+"F0.wireOp",EDGE,"E70.2")])],"isStart":false})]}),makeQuery(id+"F14.opExtrude","SWEPT_FACE",FACE,{"disambiguationData":[OSD([subQ0]),TDD([makeQuery(id+"F2.opExtrude","CAP_EDGE",EDGE,{"disambiguationData":[OSD([subQ0])],"isStart":false})])]})]});}
            extrude(context, id + "F16", {"entities" : qUnion([Q0, Q1, Q2, Q3]), "operationType" : NewBodyOperationType.ADD, "endBound" : BoundingType.UP_TO_SURFACE, "depth" : 25.4 * mm, "endBoundEntityFace" : qUnion([Q4]), "offsetDistance" : 25.4 * mm});
        }
        {
            var Q0;
            {var subQ0=sQuery(id+"F0.wireOp",EDGE,"E82");Q0=makeQuery(id+"F0.imprint","IMPRINT",FACE,{"disambiguationData":[TD([[makeQuery(id+"F0.imprint","IMPRINT",EDGE,{"derivedFrom":subQ0}),1.0]])]});}
            var Q1;
            {var subQ0=sQuery(id+"F0.wireOp",EDGE,"E69");var subQ1=sQuery(id+"F0.wireOp",EDGE,"E68");var subQ2=sQuery(id+"F0.wireOp",EDGE,"E67");var subQ3=sQuery(id+"F0.wireOp",EDGE,"E58");var subQ4=sQuery(id+"F0.wireOp",EDGE,"E53");var subQ5=sQuery(id+"F0.wireOp",EDGE,"E65");var subQ6=sQuery(id+"F0.wireOp",EDGE,"E60");var subQ7=sQuery(id+"F0.wireOp",EDGE,"E55");var subQ8=sQuery(id+"F0.wireOp",EDGE,"E20");var subQ9=sQuery(id+"F0.wireOp",EDGE,"E19");var subQ10=sQuery(id+"F0.wireOp",EDGE,"E18");var subQ11=sQuery(id+"F0.wireOp",EDGE,"E22");var subQ12=sQuery(id+"F0.wireOp",EDGE,"E21");var subQ13=sQuery(id+"F0.wireOp",EDGE,"E16");var subQ14=sQuery(id+"F0.wireOp",EDGE,"E0.bottom");var subQ15=sQuery(id+"F0.wireOp",EDGE,"E27.5");var subQ16=sQuery(id+"F0.wireOp",EDGE,"E27.4");var subQ17=sQuery(id+"F0.wireOp",EDGE,"E28.1");var subQ18=sQuery(id+"F0.wireOp",EDGE,"E28.0");var subQ19=sQuery(id+"F0.wireOp",EDGE,"E17");var subQ20=sQuery(id+"F0.wireOp",EDGE,"E28.3");var subQ21=sQuery(id+"F0.wireOp",EDGE,"E28.2");var subQ22=sQuery(id+"F0.wireOp",EDGE,"E27.1");var subQ23=sQuery(id+"F0.wireOp",EDGE,"E27.0");var subQ24=sQuery(id+"F0.wireOp",EDGE,"E27.3");var subQ25=sQuery(id+"F0.wireOp",EDGE,"E27.2");var subQ26=sQuery(id+"F0.wireOp",EDGE,"E2.bottom");var subQ27=sQuery(id+"F0.wireOp",EDGE,"E1.bottom");var subQ28=sQuery(id+"F0.wireOp",EDGE,"E15");var subQ29=sQuery(id+"F0.wireOp",EDGE,"E1.left");var subQ30=sQuery(id+"F0.wireOp",EDGE,"E2.left");Q1=makeQuery(id+"F16.boolean.opBoolean","MERGE",FACE,{"derivedFrom":[makeQuery(id+"F14.boolean.opBoolean","MERGE",FACE,{"derivedFrom":[makeQuery(id+"F11.boolean.opBoolean","MERGE",FACE,{"derivedFrom":[makeQuery(id+"F10.boolean.opBoolean","MERGE",FACE,{"derivedFrom":[makeQuery(id+"F9.boolean.opBoolean","MERGE",FACE,{"derivedFrom":[makeQuery(id+"F8.boolean.opBoolean","MERGE",FACE,{"derivedFrom":[makeQuery(id+"F7.boolean.opBoolean","MERGE",FACE,{"derivedFrom":[makeQuery(id+"F6.boolean.opBoolean","MERGE",FACE,{"derivedFrom":[makeQuery(id+"F2.boolean.opBoolean","MERGE",FACE,{"derivedFrom":[makeQuery(id+"F1.opExtrude","CAP_FACE",FACE,{"disambiguationData":[OSD([subQ26,sQuery(id+"F0.wireOp",EDGE,"E2.top"),subQ30,sQuery(id+"F0.wireOp",EDGE,"E2.right")])],"isStart":false}),makeQuery(id+"F2.opExtrude","CAP_FACE",FACE,{"disambiguationData":[OSD([subQ14,subQ30,subQ4,sQuery(id+"F0.wireOp",EDGE,"E59"),subQ6,sQuery(id+"F0.wireOp",EDGE,"E61"),sQuery(id+"F0.wireOp",EDGE,"E63"),subQ5])],"isStart":false})]}),makeQuery(id+"F5.boolean.opBoolean","MERGE",FACE,{"derivedFrom":[makeQuery(id+"F4.boolean.opBoolean","MERGE",FACE,{"derivedFrom":[makeQuery(id+"F2.boolean.opBoolean","MERGE",FACE,{"derivedFrom":[makeQuery(id+"F1.opExtrude","CAP_FACE",FACE,{"disambiguationData":[OSD([subQ27,sQuery(id+"F0.wireOp",EDGE,"E1.top"),subQ29,sQuery(id+"F0.wireOp",EDGE,"E1.right"),subQ28])],"isStart":false}),makeQuery(id+"F2.opExtrude","CAP_FACE",FACE,{"disambiguationData":[OSD([subQ14,subQ29,subQ28,sQuery(id+"F0.wireOp",EDGE,"E54"),subQ7,sQuery(id+"F0.wireOp",EDGE,"E56"),sQuery(id+"F0.wireOp",EDGE,"E57"),subQ3,sQuery(id+"F0.wireOp",EDGE,"E62"),sQuery(id+"F0.wireOp",EDGE,"E64")])],"isStart":false})]}),makeQuery(id+"F4.opExtrude","CAP_FACE",FACE,{"disambiguationData":[OSD([subQ14,subQ19,subQ8,subQ11,subQ23,subQ22,subQ25,subQ24,subQ16,subQ15,subQ18,subQ17,subQ21,subQ20])],"isStart":false})]}),makeQuery(id+"F5.opExtrude","CAP_FACE",FACE,{"disambiguationData":[OSD([subQ27,subQ26,subQ13,subQ19,subQ10,sQuery(id+"F0.wireOp",EDGE,"E29.0"),sQuery(id+"F0.wireOp",EDGE,"E30"),sQuery(id+"F0.wireOp",EDGE,"E31.0")])],"isStart":false})]}),makeQuery(id+"F6.opExtrude","CAP_FACE",FACE,{"disambiguationData":[OSD([subQ14,subQ25,subQ24,sQuery(id+"F0.wireOp",EDGE,"E41.0"),sQuery(id+"F0.wireOp",EDGE,"E42.0")])],"isStart":false}),makeQuery(id+"F6.opExtrude","CAP_FACE",FACE,{"disambiguationData":[OSD([subQ14,subQ23,subQ22,sQuery(id+"F0.wireOp",EDGE,"E43.0"),sQuery(id+"F0.wireOp",EDGE,"E44.0")])],"isStart":false}),makeQuery(id+"F6.opExtrude","CAP_FACE",FACE,{"disambiguationData":[OSD([subQ19,subQ21,subQ20,sQuery(id+"F0.wireOp",EDGE,"E37.0"),sQuery(id+"F0.wireOp",EDGE,"E38.0")])],"isStart":false}),makeQuery(id+"F6.opExtrude","CAP_FACE",FACE,{"disambiguationData":[OSD([subQ19,subQ18,subQ17,sQuery(id+"F0.wireOp",EDGE,"E39.0"),sQuery(id+"F0.wireOp",EDGE,"E40.0")])],"isStart":false})]}),makeQuery(id+"F7.opExtrude","CAP_FACE",FACE,{"disambiguationData":[OSD([subQ14,subQ16,subQ15,sQuery(id+"F0.wireOp",EDGE,"E48.0"),sQuery(id+"F0.wireOp",EDGE,"E49.0")])],"isStart":false})]}),makeQuery(id+"F8.opExtrude","CAP_FACE",FACE,{"disambiguationData":[OSD([subQ14,subQ13,subQ12,sQuery(id+"F0.wireOp",EDGE,"E51.0")])],"isStart":false}),makeQuery(id+"F8.opExtrude","CAP_FACE",FACE,{"disambiguationData":[OSD([subQ14,subQ10,subQ9,sQuery(id+"F0.wireOp",EDGE,"E50.0")])],"isStart":false})]}),makeQuery(id+"F9.opExtrude","CAP_FACE",FACE,{"disambiguationData":[OSD([subQ13,subQ12,subQ11,sQuery(id+"F0.wireOp",EDGE,"E52.0")])],"isStart":false})]}),makeQuery(id+"F10.opExtrude","CAP_FACE",FACE,{"disambiguationData":[OSD([subQ10,subQ9,subQ8,sQuery(id+"F0.wireOp",EDGE,"E66.0")])],"isStart":false})]}),makeQuery(id+"F11.opExtrude","CAP_FACE",FACE,{"disambiguationData":[OSD([subQ7,subQ6,subQ2,subQ1,subQ0,sQuery(id+"F0.wireOp",EDGE,"E70.0"),sQuery(id+"F0.wireOp",EDGE,"E70.1"),sQuery(id+"F0.wireOp",EDGE,"E70.2")])],"isStart":false})]}),makeQuery(id+"F14.opExtrude","SWEPT_FACE",FACE,{"disambiguationData":[OSD([subQ5]),TDD([makeQuery(id+"F2.opExtrude","CAP_EDGE",EDGE,{"disambiguationData":[OSD([subQ5])],"isStart":false})])]})]}),makeQuery(id+"F16.opExtrude","CAP_FACE",FACE,{"disambiguationData":[OSD([subQ4,subQ0,sQuery(id+"F0.wireOp",EDGE,"E73"),sQuery(id+"F0.wireOp",EDGE,"E76.0")])],"isStart":false}),makeQuery(id+"F16.opExtrude","CAP_FACE",FACE,{"disambiguationData":[OSD([subQ3,subQ0,sQuery(id+"F0.wireOp",EDGE,"E72"),sQuery(id+"F0.wireOp",EDGE,"E78.0")])],"isStart":false}),makeQuery(id+"F16.opExtrude","CAP_FACE",FACE,{"disambiguationData":[OSD([subQ2,subQ0,sQuery(id+"F0.wireOp",EDGE,"E71"),sQuery(id+"F0.wireOp",EDGE,"E79.0")])],"isStart":false}),makeQuery(id+"F16.opExtrude","CAP_FACE",FACE,{"disambiguationData":[OSD([subQ1,subQ0,sQuery(id+"F0.wireOp",EDGE,"E74"),sQuery(id+"F0.wireOp",EDGE,"E77.0")])],"isStart":false})]});}
            extrude(context, id + "F17", {"entities" : qUnion([Q0]), "operationType" : NewBodyOperationType.ADD, "endBound" : BoundingType.UP_TO_SURFACE, "depth" : 25.4 * mm, "endBoundEntityFace" : qUnion([Q1]), "offsetDistance" : 25.4 * mm});
        }
        {
            var Q0;
            {var subQ2=sQuery(id+"F0.wireOp",EDGE,"E73");Q0=makeQuery(id+"F0.imprint","IMPRINT",FACE,{"disambiguationData":[TD([[makeQuery(id+"F0.imprint","IMPRINT",EDGE,{"derivedFrom":subQ2}),-1.0]])]});}
            var Q1;
            {var subQ2=sQuery(id+"F0.wireOp",EDGE,"E74");Q1=makeQuery(id+"F0.imprint","IMPRINT",FACE,{"disambiguationData":[TD([[makeQuery(id+"F0.imprint","IMPRINT",EDGE,{"derivedFrom":subQ2}),-1.0]])]});}
            var Q2;
            {var subQ0=sQuery(id+"F0.wireOp",EDGE,"E71");Q2=makeQuery(id+"F0.imprint","IMPRINT",FACE,{"disambiguationData":[TD([[makeQuery(id+"F0.imprint","IMPRINT",EDGE,{"derivedFrom":subQ0}),-1.0]])]});}
            var Q3;
            {var subQ2=sQuery(id+"F0.wireOp",EDGE,"E72");Q3=makeQuery(id+"F0.imprint","IMPRINT",FACE,{"disambiguationData":[TD([[makeQuery(id+"F0.imprint","IMPRINT",EDGE,{"derivedFrom":subQ2}),-1.0]])]});}
            var Q4;
            {var subQ0=sQuery(id+"F0.wireOp",EDGE,"E69");var subQ1=sQuery(id+"F0.wireOp",EDGE,"E68");var subQ2=sQuery(id+"F0.wireOp",EDGE,"E67");var subQ3=sQuery(id+"F0.wireOp",EDGE,"E58");var subQ4=sQuery(id+"F0.wireOp",EDGE,"E53");var subQ5=sQuery(id+"F0.wireOp",EDGE,"E65");var subQ6=sQuery(id+"F0.wireOp",EDGE,"E60");var subQ7=sQuery(id+"F0.wireOp",EDGE,"E55");var subQ8=sQuery(id+"F0.wireOp",EDGE,"E20");var subQ9=sQuery(id+"F0.wireOp",EDGE,"E19");var subQ10=sQuery(id+"F0.wireOp",EDGE,"E18");var subQ11=sQuery(id+"F0.wireOp",EDGE,"E22");var subQ12=sQuery(id+"F0.wireOp",EDGE,"E21");var subQ13=sQuery(id+"F0.wireOp",EDGE,"E16");var subQ14=sQuery(id+"F0.wireOp",EDGE,"E0.bottom");var subQ15=sQuery(id+"F0.wireOp",EDGE,"E27.5");var subQ16=sQuery(id+"F0.wireOp",EDGE,"E27.4");var subQ17=sQuery(id+"F0.wireOp",EDGE,"E28.1");var subQ18=sQuery(id+"F0.wireOp",EDGE,"E28.0");var subQ19=sQuery(id+"F0.wireOp",EDGE,"E17");var subQ20=sQuery(id+"F0.wireOp",EDGE,"E28.3");var subQ21=sQuery(id+"F0.wireOp",EDGE,"E28.2");var subQ22=sQuery(id+"F0.wireOp",EDGE,"E27.1");var subQ23=sQuery(id+"F0.wireOp",EDGE,"E27.0");var subQ24=sQuery(id+"F0.wireOp",EDGE,"E27.3");var subQ25=sQuery(id+"F0.wireOp",EDGE,"E27.2");var subQ26=sQuery(id+"F0.wireOp",EDGE,"E2.bottom");var subQ27=sQuery(id+"F0.wireOp",EDGE,"E1.bottom");var subQ28=sQuery(id+"F0.wireOp",EDGE,"E15");var subQ29=sQuery(id+"F0.wireOp",EDGE,"E1.left");var subQ30=sQuery(id+"F0.wireOp",EDGE,"E2.left");Q4=makeQuery(id+"F17.boolean.opBoolean","MERGE",FACE,{"derivedFrom":[makeQuery(id+"F16.boolean.opBoolean","MERGE",FACE,{"derivedFrom":[makeQuery(id+"F14.boolean.opBoolean","MERGE",FACE,{"derivedFrom":[makeQuery(id+"F11.boolean.opBoolean","MERGE",FACE,{"derivedFrom":[makeQuery(id+"F10.boolean.opBoolean","MERGE",FACE,{"derivedFrom":[makeQuery(id+"F9.boolean.opBoolean","MERGE",FACE,{"derivedFrom":[makeQuery(id+"F8.boolean.opBoolean","MERGE",FACE,{"derivedFrom":[makeQuery(id+"F7.boolean.opBoolean","MERGE",FACE,{"derivedFrom":[makeQuery(id+"F6.boolean.opBoolean","MERGE",FACE,{"derivedFrom":[makeQuery(id+"F2.boolean.opBoolean","MERGE",FACE,{"derivedFrom":[makeQuery(id+"F1.opExtrude","CAP_FACE",FACE,{"disambiguationData":[OSD([subQ26,sQuery(id+"F0.wireOp",EDGE,"E2.top"),subQ30,sQuery(id+"F0.wireOp",EDGE,"E2.right")])],"isStart":false}),makeQuery(id+"F2.opExtrude","CAP_FACE",FACE,{"disambiguationData":[OSD([subQ14,subQ30,subQ4,sQuery(id+"F0.wireOp",EDGE,"E59"),subQ6,sQuery(id+"F0.wireOp",EDGE,"E61"),sQuery(id+"F0.wireOp",EDGE,"E63"),subQ5])],"isStart":false})]}),makeQuery(id+"F5.boolean.opBoolean","MERGE",FACE,{"derivedFrom":[makeQuery(id+"F4.boolean.opBoolean","MERGE",FACE,{"derivedFrom":[makeQuery(id+"F2.boolean.opBoolean","MERGE",FACE,{"derivedFrom":[makeQuery(id+"F1.opExtrude","CAP_FACE",FACE,{"disambiguationData":[OSD([subQ27,sQuery(id+"F0.wireOp",EDGE,"E1.top"),subQ29,sQuery(id+"F0.wireOp",EDGE,"E1.right"),subQ28])],"isStart":false}),makeQuery(id+"F2.opExtrude","CAP_FACE",FACE,{"disambiguationData":[OSD([subQ14,subQ29,subQ28,sQuery(id+"F0.wireOp",EDGE,"E54"),subQ7,sQuery(id+"F0.wireOp",EDGE,"E56"),sQuery(id+"F0.wireOp",EDGE,"E57"),subQ3,sQuery(id+"F0.wireOp",EDGE,"E62"),sQuery(id+"F0.wireOp",EDGE,"E64")])],"isStart":false})]}),makeQuery(id+"F4.opExtrude","CAP_FACE",FACE,{"disambiguationData":[OSD([subQ14,subQ19,subQ8,subQ11,subQ23,subQ22,subQ25,subQ24,subQ16,subQ15,subQ18,subQ17,subQ21,subQ20])],"isStart":false})]}),makeQuery(id+"F5.opExtrude","CAP_FACE",FACE,{"disambiguationData":[OSD([subQ27,subQ26,subQ13,subQ19,subQ10,sQuery(id+"F0.wireOp",EDGE,"E29.0"),sQuery(id+"F0.wireOp",EDGE,"E30"),sQuery(id+"F0.wireOp",EDGE,"E31.0")])],"isStart":false})]}),makeQuery(id+"F6.opExtrude","CAP_FACE",FACE,{"disambiguationData":[OSD([subQ14,subQ25,subQ24,sQuery(id+"F0.wireOp",EDGE,"E41.0"),sQuery(id+"F0.wireOp",EDGE,"E42.0")])],"isStart":false}),makeQuery(id+"F6.opExtrude","CAP_FACE",FACE,{"disambiguationData":[OSD([subQ14,subQ23,subQ22,sQuery(id+"F0.wireOp",EDGE,"E43.0"),sQuery(id+"F0.wireOp",EDGE,"E44.0")])],"isStart":false}),makeQuery(id+"F6.opExtrude","CAP_FACE",FACE,{"disambiguationData":[OSD([subQ19,subQ21,subQ20,sQuery(id+"F0.wireOp",EDGE,"E37.0"),sQuery(id+"F0.wireOp",EDGE,"E38.0")])],"isStart":false}),makeQuery(id+"F6.opExtrude","CAP_FACE",FACE,{"disambiguationData":[OSD([subQ19,subQ18,subQ17,sQuery(id+"F0.wireOp",EDGE,"E39.0"),sQuery(id+"F0.wireOp",EDGE,"E40.0")])],"isStart":false})]}),makeQuery(id+"F7.opExtrude","CAP_FACE",FACE,{"disambiguationData":[OSD([subQ14,subQ16,subQ15,sQuery(id+"F0.wireOp",EDGE,"E48.0"),sQuery(id+"F0.wireOp",EDGE,"E49.0")])],"isStart":false})]}),makeQuery(id+"F8.opExtrude","CAP_FACE",FACE,{"disambiguationData":[OSD([subQ14,subQ13,subQ12,sQuery(id+"F0.wireOp",EDGE,"E51.0")])],"isStart":false}),makeQuery(id+"F8.opExtrude","CAP_FACE",FACE,{"disambiguationData":[OSD([subQ14,subQ10,subQ9,sQuery(id+"F0.wireOp",EDGE,"E50.0")])],"isStart":false})]}),makeQuery(id+"F9.opExtrude","CAP_FACE",FACE,{"disambiguationData":[OSD([subQ13,subQ12,subQ11,sQuery(id+"F0.wireOp",EDGE,"E52.0")])],"isStart":false})]}),makeQuery(id+"F10.opExtrude","CAP_FACE",FACE,{"disambiguationData":[OSD([subQ10,subQ9,subQ8,sQuery(id+"F0.wireOp",EDGE,"E66.0")])],"isStart":false})]}),makeQuery(id+"F11.opExtrude","CAP_FACE",FACE,{"disambiguationData":[OSD([subQ7,subQ6,subQ2,subQ1,subQ0,sQuery(id+"F0.wireOp",EDGE,"E70.0"),sQuery(id+"F0.wireOp",EDGE,"E70.1"),sQuery(id+"F0.wireOp",EDGE,"E70.2")])],"isStart":false})]}),makeQuery(id+"F14.opExtrude","SWEPT_FACE",FACE,{"disambiguationData":[OSD([subQ5]),TDD([makeQuery(id+"F2.opExtrude","CAP_EDGE",EDGE,{"disambiguationData":[OSD([subQ5])],"isStart":false})])]})]}),makeQuery(id+"F16.opExtrude","CAP_FACE",FACE,{"disambiguationData":[OSD([subQ4,subQ0,sQuery(id+"F0.wireOp",EDGE,"E73"),sQuery(id+"F0.wireOp",EDGE,"E76.0")])],"isStart":false}),makeQuery(id+"F16.opExtrude","CAP_FACE",FACE,{"disambiguationData":[OSD([subQ3,subQ0,sQuery(id+"F0.wireOp",EDGE,"E72"),sQuery(id+"F0.wireOp",EDGE,"E78.0")])],"isStart":false}),makeQuery(id+"F16.opExtrude","CAP_FACE",FACE,{"disambiguationData":[OSD([subQ2,subQ0,sQuery(id+"F0.wireOp",EDGE,"E71"),sQuery(id+"F0.wireOp",EDGE,"E79.0")])],"isStart":false}),makeQuery(id+"F16.opExtrude","CAP_FACE",FACE,{"disambiguationData":[OSD([subQ1,subQ0,sQuery(id+"F0.wireOp",EDGE,"E74"),sQuery(id+"F0.wireOp",EDGE,"E77.0")])],"isStart":false})]}),makeQuery(id+"F17.opExtrude","CAP_FACE",FACE,{"disambiguationData":[OSD([subQ0,sQuery(id+"F0.wireOp",EDGE,"E75"),sQuery(id+"F0.wireOp",EDGE,"E82"),sQuery(id+"F0.wireOp",EDGE,"E83")])],"isStart":false})]});}
            extrude(context, id + "F18", {"entities" : qUnion([Q0, Q1, Q2, Q3]), "operationType" : NewBodyOperationType.ADD, "endBound" : BoundingType.UP_TO_SURFACE, "depth" : 25.4 * mm, "endBoundEntityFace" : qUnion([Q4]), "offsetDistance" : 25.4 * mm});
        }
        {
            var Q0;
            Q0=makeQuery(id+"F1.opExtrude","SWEPT_BODY",BODY,{"disambiguationData":[OSD([sQuery(id+"F0.wireOp",EDGE,"E1.bottom"),sQuery(id+"F0.wireOp",EDGE,"E1.top"),sQuery(id+"F0.wireOp",EDGE,"E1.left"),sQuery(id+"F0.wireOp",EDGE,"E1.right"),sQuery(id+"F0.wireOp",EDGE,"E15")])]});
            var Q1;
            {var subQ0=sQuery(id+"F0.wireOp",EDGE,"E15");var subQ1=sQuery(id+"F0.wireOp",EDGE,"E1.left");Q1=makeQuery(id+"F2.boolean.opBoolean","MERGE",FACE,{"derivedFrom":[makeQuery(id+"F1.opExtrude","CAP_FACE",FACE,{"disambiguationData":[OSD([sQuery(id+"F0.wireOp",EDGE,"E1.bottom"),sQuery(id+"F0.wireOp",EDGE,"E1.top"),subQ1,sQuery(id+"F0.wireOp",EDGE,"E1.right"),subQ0])],"isStart":true}),makeQuery(id+"F2.opExtrude","CAP_FACE",FACE,{"disambiguationData":[OSD([sQuery(id+"F0.wireOp",EDGE,"E0.bottom"),subQ1,subQ0,sQuery(id+"F0.wireOp",EDGE,"E54"),sQuery(id+"F0.wireOp",EDGE,"E55"),sQuery(id+"F0.wireOp",EDGE,"E56"),sQuery(id+"F0.wireOp",EDGE,"E57"),sQuery(id+"F0.wireOp",EDGE,"E58"),sQuery(id+"F0.wireOp",EDGE,"E62"),sQuery(id+"F0.wireOp",EDGE,"E64")])],"isStart":true})]});}
            mirror(context, id + "F19", {"operationType" : NewBodyOperationType.ADD, "entities" : qUnion([Q0]), "mirrorPlane" : qUnion([Q1])});
        }
        {
            var Q0;
            Q0=makeQuery(id+"F12.imprint","IMPRINT",FACE,{"disambiguationData":[TD([[makeQuery(id+"F12.imprint","IMPRINT",EDGE,{"derivedFrom":sQuery(id+"F12.wireOp",EDGE,"E84.bottom")}),-1.0]])]});
            var Q1;
            Q1=makeQuery(id+"F12.imprint","IMPRINT",FACE,{"disambiguationData":[TD([[makeQuery(id+"F12.imprint","IMPRINT",EDGE,{"derivedFrom":sQuery(id+"F12.wireOp",EDGE,"E85.top")}),-1.0]])]});
            var Q2;
            Q2=makeQuery(id+"F12.imprint","IMPRINT",FACE,{"disambiguationData":[TD([[makeQuery(id+"F12.imprint","IMPRINT",EDGE,{"derivedFrom":sQuery(id+"F12.wireOp",EDGE,"E86.bottom")}),-1.0]])]});
            var Q3;
            Q3=makeQuery(id+"F12.imprint","IMPRINT",FACE,{"disambiguationData":[TD([[makeQuery(id+"F12.imprint","IMPRINT",EDGE,{"derivedFrom":sQuery(id+"F12.wireOp",EDGE,"E87.bottom")}),-1.0]])]});
            var Q4;
            Q4=makeQuery(id+"F12.imprint","IMPRINT",FACE,{"disambiguationData":[TD([[makeQuery(id+"F12.imprint","IMPRINT",EDGE,{"derivedFrom":sQuery(id+"F12.wireOp",EDGE,"E88.bottom")}),-1.0]])]});
            extrude(context, id + "F20", {"entities" : qUnion([Q0, Q1, Q2, Q3, Q4]), "operationType" : NewBodyOperationType.ADD, "endBound" : BoundingType.UP_TO_NEXT, "oppositeDirection" : true, "depth" : 25.4 * mm, "offsetDistance" : 25.4 * mm});
        }
        {
            var Q0;
            {var subQ7=sQuery(id+"F0.wireOp",EDGE,"E70.0");Q0=makeQuery(id+"F0.imprint","IMPRINT",FACE,{"disambiguationData":[TD([[makeQuery(id+"F0.imprint","IMPRINT",EDGE,{"derivedFrom":subQ7}),1.0]])]});}
            extrude(context, id + "F21", {"entities" : qUnion([Q0]), "operationType" : NewBodyOperationType.ADD, "endBound" : BoundingType.UP_TO_NEXT, "oppositeDirection" : true, "depth" : 25.4 * mm, "offsetDistance" : 25.4 * mm});
        }
        {
            var Q0;
            {var subQ16=sQuery(id+"F13.wireOp",EDGE,"E89.bottom");Q0=makeQuery(id+"F13.imprint","IMPRINT",FACE,{"disambiguationData":[TD([[makeQuery(id+"F13.imprint","IMPRINT",EDGE,{"derivedFrom":subQ16}),-1.0]])]});}
            var Q1;
            {var subQ4=sQuery(id+"F0.wireOp",EDGE,"E0.bottom");var subQ14=makeQuery(id+"F0.imprint","INTERSECT",VERTEX,{"derivedFrom":[subQ4,sQuery(id+"F0.wireOp",EDGE,"E65")]});var subQ17=makeQuery(id+"F0.imprint","INTERSECT",VERTEX,{"derivedFrom":[subQ4,sQuery(id+"F0.wireOp",EDGE,"E49.0")]});var subQ18=makeQuery(id+"F0.imprint","IMPRINT",EDGE,{"disambiguationData":[TD([[subQ17,1.0]])],"derivedFrom":subQ4});var subQ19=makeQuery(id+"F0.imprint","IMPRINT",EDGE,{"disambiguationData":[TD([[subQ14,1.0]])],"derivedFrom":subQ4});var subQ22=makeQuery(id+"F3.opExtrude","CAP_EDGE",EDGE,{"disambiguationData":[OSD([subQ4]),TDD([subQ19,subQ18])],"isStart":true});Q1=makeQuery(id+"F13.imprint","IMPRINT",FACE,{"disambiguationData":[TD([[makeQuery(id+"F13.imprint","IMPRINT",EDGE,{"derivedFrom":subQ22}),-1.0]])]});}
            extrude(context, id + "F22", {"entities" : qUnion([Q0, Q1]), "operationType" : NewBodyOperationType.REMOVE, "endBound" : BoundingType.THROUGH_ALL, "oppositeDirection" : true, "depth" : 25.4 * mm, "offsetDistance" : 25.4 * mm});
        }
    });
